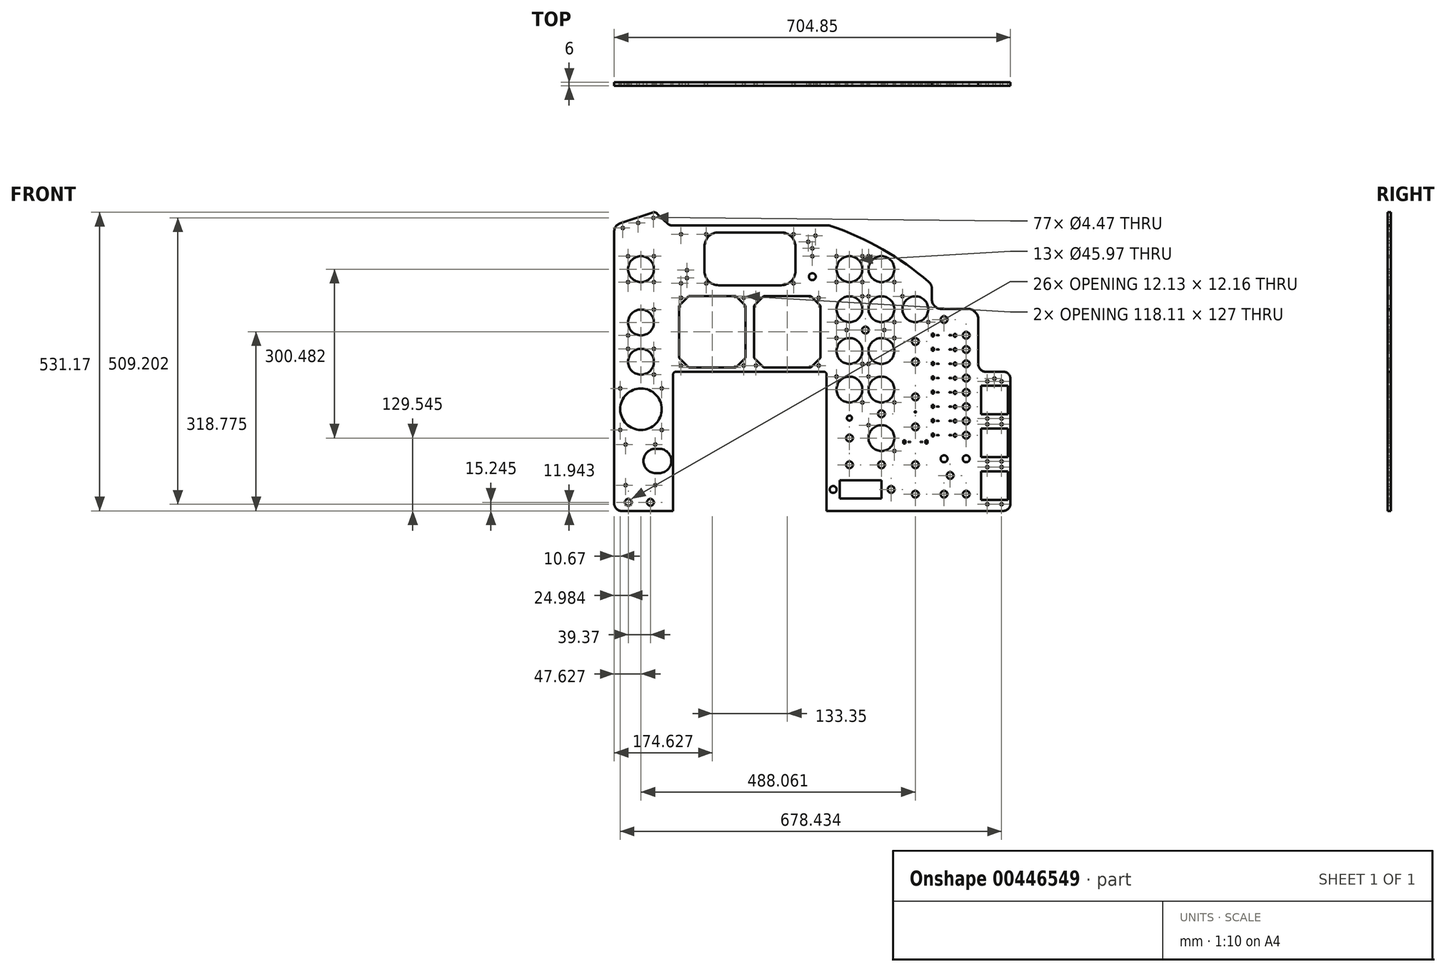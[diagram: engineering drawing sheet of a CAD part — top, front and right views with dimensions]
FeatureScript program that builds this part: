
annotation { "Feature Type Name" : "Feature", "Feature Type Description" : "" }
export const myFeature = defineFeature(function(context is Context, id is Id, definition is map)
    precondition{}
    {
        {
            var Q0;
            Q0=qCreatedBy(makeId("Front.planeOp"),FACE);
            var sketch = newSketch(context, id + "F0", { "sketchPlane" : qUnion([Q0])});
            skLineSegment(sketch, "E0", {"start": v(-241.06, -131.64) * mm, "end": v(-148.98, -131.64) * mm});
            skLineSegment(sketch, "E1", {"start": v(-148.98, -131.64) * mm, "end": v(-148.98, 110.93) * mm});
            skLineSegment(sketch, "E2", {"start": v(-143.9, 116.01) * mm, "end": v(118.99, 116.01) * mm});
            skLineSegment(sketch, "E3", {"start": v(124.07, 110.93) * mm, "end": v(124.07, -131.64) * mm});
            skLineSegment(sketch, "E4", {"start": v(124.07, -131.64) * mm, "end": v(311.4, -131.64) * mm});
            skLineSegment(sketch, "E5", {"start": v(-253.76, 255.71) * mm, "end": v(-253.76, -118.94) * mm});
            skLineSegment(sketch, "E6", {"start": v(-152.8, 376.44) * mm, "end": v(117.72, 376.44) * mm});
            skLineSegment(sketch, "E7", {"start": v(-253.76, 255.71) * mm, "end": v(-253.76, 365.43) * mm});
            skLineSegment(sketch, "E8", {"start": v(311.4, -131.64) * mm, "end": v(438.4, -131.64) * mm});
            skLineSegment(sketch, "E9", {"start": v(451.1, -118.94) * mm, "end": v(451.1, 103.31) * mm});
            skLineSegment(sketch, "E10", {"start": v(438.4, 116.01) * mm, "end": v(406.64, 116.01) * mm});
            skLineSegment(sketch, "E11", {"start": v(393.94, 128.71) * mm, "end": v(393.94, 208.72) * mm});
            skLineSegment(sketch, "E12", {"start": v(374.9, 227.77) * mm, "end": v(327.9, 227.77) * mm});
            skLineSegment(sketch, "E13", {"start": v(-243.3, 379.9) * mm, "end": v(-185.23, 399.14) * mm});
            skLineSegment(sketch, "E14", {"start": v(-157.17, 378.17) * mm, "end": v(-177.6, 397.45) * mm});
            skLineSegment(sketch, "E15", {"start": v(117.72, 376.44) * mm, "end": v(123.7, 376.44) * mm});
            skLineSegment(sketch, "E16", {"start": v(311.4, 255.71) * mm, "end": v(311.4, 263.42) * mm});
            skLineSegment(sketch, "E17", {"start": v(-253.76, 376.44) * mm, "end": v(-155.33, 376.44) * mm, "construction": true});
            skLineSegment(sketch, "E18", {"start": v(-180.91, 400.57) * mm, "end": v(-180.91, 376.44) * mm, "construction": true});
            skLineSegment(sketch, "E19", {"start": v(217.5, 323.68) * mm, "end": v(223.32, 333.8) * mm, "construction": true});
            skArc(sketch, "E20", {"start": v(305.6, 275.97) * mm, "mid": v(223.45, 333.73) * mm, "end": v(131.93, 375.07) * mm});
            skLineSegment(sketch, "E21", {"start": v(127.88, 376.44) * mm, "end": v(311.4, 270.95) * mm, "construction": true});
            skPoint(sketch, "E22.visualSharp", {"position": v(451.1, -131.64) * mm});
            skArc(sketch, "E22.filletArc", {"start": v(438.4, -131.64) * mm, "mid": v(447.37, -127.92) * mm, "end": v(451.1, -118.94) * mm});
            skPoint(sketch, "E23.visualSharp", {"position": v(451.1, 116.01) * mm});
            skArc(sketch, "E23.filletArc", {"start": v(451.1, 103.31) * mm, "mid": v(447.37, 112.3) * mm, "end": v(438.4, 116.01) * mm});
            skPoint(sketch, "E24.visualSharp", {"position": v(393.94, 116.01) * mm});
            skArc(sketch, "E24.filletArc", {"start": v(393.94, 128.71) * mm, "mid": v(397.66, 119.73) * mm, "end": v(406.64, 116.01) * mm});
            skPoint(sketch, "E25.visualSharp", {"position": v(393.94, 227.77) * mm});
            skArc(sketch, "E25.filletArc", {"start": v(393.94, 208.72) * mm, "mid": v(388.36, 222.2) * mm, "end": v(374.9, 227.77) * mm});
            skPoint(sketch, "E26.visualSharp", {"position": v(124.07, 116.01) * mm});
            skArc(sketch, "E26.filletArc", {"start": v(124.07, 110.93) * mm, "mid": v(122.58, 114.53) * mm, "end": v(118.99, 116.01) * mm});
            skPoint(sketch, "E27.visualSharp", {"position": v(-148.98, 116.01) * mm});
            skArc(sketch, "E27.filletArc", {"start": v(-143.9, 116.01) * mm, "mid": v(-147.5, 114.53) * mm, "end": v(-148.98, 110.93) * mm});
            skPoint(sketch, "E28.visualSharp", {"position": v(-253.76, -131.64) * mm});
            skArc(sketch, "E28.filletArc", {"start": v(-253.76, -118.94) * mm, "mid": v(-250.04, -127.92) * mm, "end": v(-241.06, -131.64) * mm});
            skPoint(sketch, "E29.visualSharp", {"position": v(-155.33, 376.44) * mm});
            skArc(sketch, "E29.filletArc", {"start": v(-157.17, 378.17) * mm, "mid": v(-155.15, 376.89) * mm, "end": v(-152.8, 376.44) * mm});
            skPoint(sketch, "E30.visualSharp", {"position": v(-180.91, 400.57) * mm});
            skArc(sketch, "E30.filletArc", {"start": v(-177.6, 397.45) * mm, "mid": v(-181.18, 399.35) * mm, "end": v(-185.23, 399.14) * mm});
            skPoint(sketch, "E31.visualSharp", {"position": v(-253.76, 376.44) * mm});
            skArc(sketch, "E31.filletArc", {"start": v(-243.3, 379.9) * mm, "mid": v(-250.87, 374.36) * mm, "end": v(-253.76, 365.43) * mm});
            skLineSegment(sketch, "E32", {"start": v(311.4, 255.71) * mm, "end": v(311.4, 244.28) * mm});
            skPoint(sketch, "E33.visualSharp", {"position": v(311.4, 227.77) * mm});
            skArc(sketch, "E33.filletArc", {"start": v(311.4, 244.28) * mm, "mid": v(316.23, 232.61) * mm, "end": v(327.9, 227.77) * mm});
            skPoint(sketch, "E34.visualSharp", {"position": v(311.4, 270.95) * mm});
            skArc(sketch, "E34.filletArc", {"start": v(311.4, 263.42) * mm, "mid": v(309.88, 270.33) * mm, "end": v(305.6, 275.97) * mm});
            skPoint(sketch, "E35.visualSharp", {"position": v(127.88, 376.44) * mm});
            skArc(sketch, "E35.filletArc", {"start": v(131.93, 375.07) * mm, "mid": v(127.87, 376.1) * mm, "end": v(123.7, 376.44) * mm});
            skLineSegment(sketch, "E36", {"start": v(-206.13, -131.64) * mm, "end": v(-206.13, 376.44) * mm, "construction": true});
            skCircle(sketch, "E37", {"center": v(-206.13, 49.34) * mm, "radius": 36.96 * mm});
            skCircle(sketch, "E38", {"center": v(-206.13, 133.67) * mm, "radius": 22.99 * mm});
            skCircle(sketch, "E39", {"center": v(-206.13, 203.52) * mm, "radius": 22.99 * mm});
            skCircle(sketch, "E40", {"center": v(-206.13, 298.39) * mm, "radius": 22.99 * mm});
            skLineSegment(sketch, "E41", {"start": v(164.7, -131.64) * mm, "end": v(164.7, 355.27) * mm, "construction": true});
            skLineSegment(sketch, "E42", {"start": v(221.6, -131.64) * mm, "end": v(221.6, 322.57) * mm, "construction": true});
            skLineSegment(sketch, "E43", {"start": v(281.93, -131.64) * mm, "end": v(281.93, 287.9) * mm, "construction": true});
            skCircle(sketch, "E44", {"center": v(164.7, 84.26) * mm, "radius": 22.99 * mm});
            skCircle(sketch, "E45", {"center": v(164.7, 152.84) * mm, "radius": 22.99 * mm});
            skCircle(sketch, "E46", {"center": v(221.6, 152.84) * mm, "radius": 22.99 * mm});
            skCircle(sketch, "E47", {"center": v(221.6, 84.26) * mm, "radius": 22.99 * mm});
            skCircle(sketch, "E48", {"center": v(164.7, 227.14) * mm, "radius": 22.99 * mm});
            skCircle(sketch, "E49", {"center": v(221.6, 227.14) * mm, "radius": 22.99 * mm});
            skCircle(sketch, "E50", {"center": v(164.7, 298.39) * mm, "radius": 22.99 * mm});
            skCircle(sketch, "E51", {"center": v(221.6, 298.39) * mm, "radius": 22.99 * mm});
            skCircle(sketch, "E52", {"center": v(281.93, 227.14) * mm, "radius": 22.99 * mm});
            skLineSegment(sketch, "E53", {"start": v(372.35, -131.64) * mm, "end": v(372.35, 227.77) * mm, "construction": true});
            skLineSegment(sketch, "E54", {"start": v(332.98, -131.64) * mm, "end": v(332.98, 227.77) * mm, "construction": true});
            skLineSegment(sketch, "E55", {"start": v(435.34, -131.64) * mm, "end": v(435.34, 116.01) * mm, "construction": true});
            skLineSegment(sketch, "E56", {"start": v(409.94, -131.64) * mm, "end": v(409.94, 116.01) * mm, "construction": true});
            skArc(sketch, "E57", {"start": v(378.38, 3.93) * mm, "mid": v(366.25, 2.98) * mm, "end": v(378.38, 2.03) * mm});
            skArc(sketch, "E58.0.1.0", {"start": v(378.38, 29.33) * mm, "mid": v(366.25, 28.38) * mm, "end": v(378.38, 27.43) * mm});
            skArc(sketch, "E58.0.2.0", {"start": v(378.38, 54.73) * mm, "mid": v(366.25, 53.78) * mm, "end": v(378.38, 52.83) * mm});
            skArc(sketch, "E58.0.3.0", {"start": v(378.38, 80.13) * mm, "mid": v(366.25, 79.18) * mm, "end": v(378.38, 78.23) * mm});
            skArc(sketch, "E58.0.4.0", {"start": v(378.38, 105.53) * mm, "mid": v(366.25, 104.58) * mm, "end": v(378.38, 103.63) * mm});
            skArc(sketch, "E58.0.5.0", {"start": v(378.38, 130.93) * mm, "mid": v(366.25, 129.98) * mm, "end": v(378.38, 129.03) * mm});
            skArc(sketch, "E58.0.6.0", {"start": v(378.38, 156.33) * mm, "mid": v(366.25, 155.38) * mm, "end": v(378.38, 154.43) * mm});
            skArc(sketch, "E58.0.7.0", {"start": v(378.38, 181.73) * mm, "mid": v(366.25, 180.78) * mm, "end": v(378.38, 179.83) * mm});
            skLineSegment(sketch, "E58.direction1", {"start": v(372.35, 2.98) * mm, "end": v(397.75, 2.98) * mm, "construction": true});
            skLineSegment(sketch, "E58.direction2", {"start": v(372.35, 2.98) * mm, "end": v(372.35, 28.38) * mm, "construction": true});
            skCircle(sketch, "E59", {"center": v(321.8, 2.98) * mm, "radius": 3.77 * mm, "construction": true});
            skCircle(sketch, "E60.0.1.0", {"center": v(321.8, 28.38) * mm, "radius": 3.77 * mm, "construction": true});
            skCircle(sketch, "E60.0.2.0", {"center": v(321.8, 53.78) * mm, "radius": 3.77 * mm, "construction": true});
            skCircle(sketch, "E60.0.3.0", {"center": v(321.8, 79.18) * mm, "radius": 3.77 * mm, "construction": true});
            skCircle(sketch, "E60.0.4.0", {"center": v(321.8, 104.58) * mm, "radius": 3.77 * mm, "construction": true});
            skCircle(sketch, "E60.0.5.0", {"center": v(321.8, 129.98) * mm, "radius": 3.77 * mm, "construction": true});
            skCircle(sketch, "E60.0.6.0", {"center": v(321.8, 155.38) * mm, "radius": 3.77 * mm, "construction": true});
            skCircle(sketch, "E60.0.7.0", {"center": v(321.8, 180.78) * mm, "radius": 3.77 * mm, "construction": true});
            skCircle(sketch, "E60.1.0.0", {"center": v(344.16, 2.98) * mm, "radius": 3.77 * mm, "construction": true});
            skCircle(sketch, "E60.1.1.0", {"center": v(344.16, 28.38) * mm, "radius": 3.77 * mm, "construction": true});
            skCircle(sketch, "E60.1.2.0", {"center": v(344.16, 53.78) * mm, "radius": 3.77 * mm, "construction": true});
            skCircle(sketch, "E60.1.3.0", {"center": v(344.16, 79.18) * mm, "radius": 3.77 * mm, "construction": true});
            skCircle(sketch, "E60.1.4.0", {"center": v(344.16, 104.58) * mm, "radius": 3.77 * mm, "construction": true});
            skCircle(sketch, "E60.1.5.0", {"center": v(344.16, 129.98) * mm, "radius": 3.77 * mm, "construction": true});
            skCircle(sketch, "E60.1.6.0", {"center": v(344.16, 155.38) * mm, "radius": 3.77 * mm, "construction": true});
            skCircle(sketch, "E60.1.7.0", {"center": v(344.16, 180.78) * mm, "radius": 3.77 * mm, "construction": true});
            skLineSegment(sketch, "E60.direction1", {"start": v(321.8, 2.98) * mm, "end": v(344.16, 2.98) * mm, "construction": true});
            skLineSegment(sketch, "E60.direction2", {"start": v(321.8, 2.98) * mm, "end": v(321.8, 28.38) * mm, "construction": true});
            skLineSegment(sketch, "E61.bottom", {"start": v(-68.02, 363.74) * mm, "end": v(43.1, 363.74) * mm});
            skLineSegment(sketch, "E61.top", {"start": v(-68.02, 269.76) * mm, "end": v(43.1, 269.76) * mm});
            skLineSegment(sketch, "E61.left", {"start": v(-93.42, 338.34) * mm, "end": v(-93.42, 295.16) * mm});
            skLineSegment(sketch, "E61.right", {"start": v(68.5, 338.34) * mm, "end": v(68.5, 295.16) * mm});
            skLineSegment(sketch, "E62", {"start": v(-12.46, 116.01) * mm, "end": v(-12.46, 376.44) * mm, "construction": true});
            skPoint(sketch, "E63.visualSharp", {"position": v(-93.42, 363.74) * mm});
            skArc(sketch, "E63.filletArc", {"start": v(-68.02, 363.74) * mm, "mid": v(-85.98, 356.3) * mm, "end": v(-93.42, 338.34) * mm});
            skPoint(sketch, "E64.visualSharp", {"position": v(-93.42, 269.76) * mm});
            skArc(sketch, "E64.filletArc", {"start": v(-93.42, 295.16) * mm, "mid": v(-85.98, 277.2) * mm, "end": v(-68.02, 269.76) * mm});
            skPoint(sketch, "E65.visualSharp", {"position": v(68.5, 363.74) * mm});
            skArc(sketch, "E65.filletArc", {"start": v(68.5, 338.34) * mm, "mid": v(61.07, 356.3) * mm, "end": v(43.1, 363.74) * mm});
            skPoint(sketch, "E66.visualSharp", {"position": v(68.5, 269.76) * mm});
            skArc(sketch, "E66.filletArc", {"start": v(43.1, 269.76) * mm, "mid": v(61.07, 277.2) * mm, "end": v(68.5, 295.16) * mm});
            skLineSegment(sketch, "E67", {"start": v(113.27, 123.63) * mm, "end": v(96, 123.63) * mm, "construction": true});
            skLineSegment(sketch, "E68", {"start": v(113.27, 123.63) * mm, "end": v(113.27, 140.9) * mm, "construction": true});
            skLineSegment(sketch, "E69", {"start": v(113.27, 250.63) * mm, "end": v(113.27, 233.36) * mm, "construction": true});
            skLineSegment(sketch, "E70", {"start": v(113.27, 250.63) * mm, "end": v(96, 250.63) * mm, "construction": true});
            skLineSegment(sketch, "E71", {"start": v(-4.84, 250.63) * mm, "end": v(12.43, 250.63) * mm, "construction": true});
            skLineSegment(sketch, "E72", {"start": v(-4.84, 250.63) * mm, "end": v(-4.84, 233.36) * mm, "construction": true});
            skLineSegment(sketch, "E73", {"start": v(-4.84, 123.63) * mm, "end": v(-4.84, 140.9) * mm, "construction": true});
            skLineSegment(sketch, "E74", {"start": v(-4.84, 123.63) * mm, "end": v(12.43, 123.63) * mm, "construction": true});
            skLineSegment(sketch, "E75", {"start": v(12.43, 123.63) * mm, "end": v(96, 123.63) * mm});
            skLineSegment(sketch, "E76", {"start": v(113.27, 140.9) * mm, "end": v(96, 123.63) * mm});
            skLineSegment(sketch, "E77", {"start": v(113.27, 233.36) * mm, "end": v(113.27, 140.9) * mm});
            skLineSegment(sketch, "E78", {"start": v(113.27, 233.36) * mm, "end": v(96, 250.63) * mm});
            skLineSegment(sketch, "E79", {"start": v(96, 250.63) * mm, "end": v(12.43, 250.63) * mm});
            skLineSegment(sketch, "E80", {"start": v(-4.84, 233.36) * mm, "end": v(-4.84, 140.9) * mm});
            skLineSegment(sketch, "E81", {"start": v(-4.84, 140.9) * mm, "end": v(12.43, 123.63) * mm});
            skLineSegment(sketch, "E82", {"start": v(-4.84, 233.36) * mm, "end": v(12.43, 250.63) * mm});
            skLineSegment(sketch, "E83", {"start": v(-20.08, 123.63) * mm, "end": v(-37.35, 123.63) * mm, "construction": true});
            skLineSegment(sketch, "E84", {"start": v(-20.08, 123.63) * mm, "end": v(-20.08, 140.9) * mm, "construction": true});
            skLineSegment(sketch, "E85", {"start": v(-20.08, 250.63) * mm, "end": v(-20.08, 233.36) * mm, "construction": true});
            skLineSegment(sketch, "E86", {"start": v(-20.08, 250.63) * mm, "end": v(-37.35, 250.63) * mm, "construction": true});
            skLineSegment(sketch, "E87", {"start": v(-138.19, 250.63) * mm, "end": v(-120.92, 250.63) * mm, "construction": true});
            skLineSegment(sketch, "E88", {"start": v(-138.19, 250.63) * mm, "end": v(-138.19, 233.36) * mm, "construction": true});
            skLineSegment(sketch, "E89", {"start": v(-138.19, 123.63) * mm, "end": v(-138.19, 140.9) * mm, "construction": true});
            skLineSegment(sketch, "E90", {"start": v(-138.19, 123.63) * mm, "end": v(-120.92, 123.63) * mm, "construction": true});
            skLineSegment(sketch, "E91", {"start": v(-120.92, 123.63) * mm, "end": v(-37.35, 123.63) * mm});
            skLineSegment(sketch, "E92", {"start": v(-20.08, 140.9) * mm, "end": v(-37.35, 123.63) * mm});
            skLineSegment(sketch, "E93", {"start": v(-20.08, 233.36) * mm, "end": v(-20.08, 140.9) * mm});
            skLineSegment(sketch, "E94", {"start": v(-20.08, 233.36) * mm, "end": v(-37.35, 250.63) * mm});
            skLineSegment(sketch, "E95", {"start": v(-37.35, 250.63) * mm, "end": v(-120.92, 250.63) * mm});
            skLineSegment(sketch, "E96", {"start": v(-138.19, 233.36) * mm, "end": v(-138.19, 140.9) * mm});
            skLineSegment(sketch, "E97", {"start": v(-138.19, 140.9) * mm, "end": v(-120.92, 123.63) * mm});
            skLineSegment(sketch, "E98", {"start": v(-138.19, 233.36) * mm, "end": v(-120.92, 250.63) * mm});
            skLineSegment(sketch, "E99.bottom", {"start": v(354.57, 13.97) * mm, "end": v(311.4, 13.97) * mm, "construction": true});
            skLineSegment(sketch, "E99.top", {"start": v(354.57, -8) * mm, "end": v(311.4, -8) * mm, "construction": true});
            skLineSegment(sketch, "E99.left", {"start": v(354.57, 13.97) * mm, "end": v(354.57, -8) * mm, "construction": true});
            skLineSegment(sketch, "E99.right", {"start": v(311.4, 13.97) * mm, "end": v(311.4, -8) * mm, "construction": true});
            skPoint(sketch, "E99.middle", {"position": v(332.98, 2.98) * mm});
            skLineSegment(sketch, "E100.0.1.0", {"start": v(354.57, 39.37) * mm, "end": v(311.4, 39.37) * mm, "construction": true});
            skLineSegment(sketch, "E100.0.1.1", {"start": v(354.57, 39.37) * mm, "end": v(354.57, 17.4) * mm, "construction": true});
            skLineSegment(sketch, "E100.0.1.2", {"start": v(354.57, 17.4) * mm, "end": v(311.4, 17.4) * mm, "construction": true});
            skLineSegment(sketch, "E100.0.1.3", {"start": v(311.4, 39.37) * mm, "end": v(311.4, 17.4) * mm, "construction": true});
            skLineSegment(sketch, "E100.0.2.0", {"start": v(354.57, 64.77) * mm, "end": v(311.4, 64.77) * mm, "construction": true});
            skLineSegment(sketch, "E100.0.2.1", {"start": v(354.57, 64.77) * mm, "end": v(354.57, 42.8) * mm, "construction": true});
            skLineSegment(sketch, "E100.0.2.2", {"start": v(354.57, 42.8) * mm, "end": v(311.4, 42.8) * mm, "construction": true});
            skLineSegment(sketch, "E100.0.2.3", {"start": v(311.4, 64.77) * mm, "end": v(311.4, 42.8) * mm, "construction": true});
            skLineSegment(sketch, "E100.0.3.0", {"start": v(354.57, 90.17) * mm, "end": v(311.4, 90.17) * mm, "construction": true});
            skLineSegment(sketch, "E100.0.3.1", {"start": v(354.57, 90.17) * mm, "end": v(354.57, 68.2) * mm, "construction": true});
            skLineSegment(sketch, "E100.0.3.2", {"start": v(354.57, 68.2) * mm, "end": v(311.4, 68.2) * mm, "construction": true});
            skLineSegment(sketch, "E100.0.3.3", {"start": v(311.4, 90.17) * mm, "end": v(311.4, 68.2) * mm, "construction": true});
            skLineSegment(sketch, "E100.0.4.0", {"start": v(354.57, 115.57) * mm, "end": v(311.4, 115.57) * mm, "construction": true});
            skLineSegment(sketch, "E100.0.4.1", {"start": v(354.57, 115.57) * mm, "end": v(354.57, 93.6) * mm, "construction": true});
            skLineSegment(sketch, "E100.0.4.2", {"start": v(354.57, 93.6) * mm, "end": v(311.4, 93.6) * mm, "construction": true});
            skLineSegment(sketch, "E100.0.4.3", {"start": v(311.4, 115.57) * mm, "end": v(311.4, 93.6) * mm, "construction": true});
            skLineSegment(sketch, "E100.0.5.0", {"start": v(354.57, 140.97) * mm, "end": v(311.4, 140.97) * mm, "construction": true});
            skLineSegment(sketch, "E100.0.5.1", {"start": v(354.57, 140.97) * mm, "end": v(354.57, 119) * mm, "construction": true});
            skLineSegment(sketch, "E100.0.5.2", {"start": v(354.57, 119) * mm, "end": v(311.4, 119) * mm, "construction": true});
            skLineSegment(sketch, "E100.0.5.3", {"start": v(311.4, 140.97) * mm, "end": v(311.4, 119) * mm, "construction": true});
            skLineSegment(sketch, "E100.0.6.0", {"start": v(354.57, 166.37) * mm, "end": v(311.4, 166.37) * mm, "construction": true});
            skLineSegment(sketch, "E100.0.6.1", {"start": v(354.57, 166.37) * mm, "end": v(354.57, 144.4) * mm, "construction": true});
            skLineSegment(sketch, "E100.0.6.2", {"start": v(354.57, 144.4) * mm, "end": v(311.4, 144.4) * mm, "construction": true});
            skLineSegment(sketch, "E100.0.6.3", {"start": v(311.4, 166.37) * mm, "end": v(311.4, 144.4) * mm, "construction": true});
            skLineSegment(sketch, "E100.0.7.0", {"start": v(354.57, 191.77) * mm, "end": v(311.4, 191.77) * mm, "construction": true});
            skLineSegment(sketch, "E100.0.7.1", {"start": v(354.57, 191.77) * mm, "end": v(354.57, 169.8) * mm, "construction": true});
            skLineSegment(sketch, "E100.0.7.2", {"start": v(354.57, 169.8) * mm, "end": v(311.4, 169.8) * mm, "construction": true});
            skLineSegment(sketch, "E100.0.7.3", {"start": v(311.4, 191.77) * mm, "end": v(311.4, 169.8) * mm, "construction": true});
            skLineSegment(sketch, "E100.direction1", {"start": v(311.4, -8) * mm, "end": v(336.8, -8) * mm, "construction": true});
            skLineSegment(sketch, "E100.direction2", {"start": v(311.4, -8) * mm, "end": v(311.4, 17.4) * mm, "construction": true});
            skLineSegment(sketch, "E101.bottom", {"start": v(421.12, -112.08) * mm, "end": v(398.77, -112.08) * mm});
            skLineSegment(sketch, "E101.top", {"start": v(421.12, -61.28) * mm, "end": v(398.77, -61.28) * mm});
            skLineSegment(sketch, "E101.right", {"start": v(398.77, -112.08) * mm, "end": v(398.77, -61.28) * mm});
            skPoint(sketch, "E101.middle", {"position": v(409.94, -86.68) * mm});
            skPoint(sketch, "E102.0.1.0", {"position": v(409.94, -10.48) * mm});
            skLineSegment(sketch, "E102.0.1.2", {"start": v(398.77, -35.88) * mm, "end": v(398.77, 14.92) * mm});
            skPoint(sketch, "E102.0.2.0", {"position": v(409.94, 65.72) * mm});
            skLineSegment(sketch, "E102.0.2.2", {"start": v(398.77, 40.32) * mm, "end": v(398.77, 91.12) * mm});
            skPoint(sketch, "E102.1.0.0", {"position": v(435.34, -86.68) * mm});
            skLineSegment(sketch, "E102.1.0.1", {"start": v(446.52, -112.08) * mm, "end": v(446.52, -61.28) * mm});
            skPoint(sketch, "E102.1.1.0", {"position": v(435.34, -10.48) * mm});
            skLineSegment(sketch, "E102.1.1.1", {"start": v(446.52, -35.88) * mm, "end": v(446.52, 14.92) * mm});
            skPoint(sketch, "E102.1.2.0", {"position": v(435.34, 65.72) * mm});
            skLineSegment(sketch, "E102.1.2.1", {"start": v(446.52, 40.32) * mm, "end": v(446.52, 91.12) * mm});
            skLineSegment(sketch, "E102.direction1", {"start": v(398.77, -112.08) * mm, "end": v(424.17, -112.08) * mm, "construction": true});
            skLineSegment(sketch, "E102.direction2", {"start": v(398.77, -112.08) * mm, "end": v(398.77, -35.88) * mm, "construction": true});
            skArc(sketch, "E103", {"start": v(-183.34, -115.45) * mm, "mid": v(-195.47, -116.4) * mm, "end": v(-183.34, -117.35) * mm});
            skArc(sketch, "E104", {"start": v(-222.71, -115.45) * mm, "mid": v(-234.84, -116.4) * mm, "end": v(-222.71, -117.35) * mm});
            skLineSegment(sketch, "E105", {"start": v(-148.98, -116.4) * mm, "end": v(-253.76, -116.4) * mm, "construction": true});
            skLineSegment(sketch, "E106", {"start": v(124.07, 84.26) * mm, "end": v(281.93, 84.26) * mm, "construction": true});
            skLineSegment(sketch, "E107", {"start": v(281.93, 152.84) * mm, "end": v(125.15, 152.84) * mm, "construction": true});
            skLineSegment(sketch, "E108", {"start": v(281.93, 227.14) * mm, "end": v(116.2, 227.14) * mm, "construction": true});
            skArc(sketch, "E109", {"start": v(339, 209.67) * mm, "mid": v(326.88, 208.72) * mm, "end": v(339, 207.77) * mm});
            skLineSegment(sketch, "E110", {"start": v(281.93, -101.92) * mm, "end": v(451.1, -101.92) * mm, "construction": true});
            skArc(sketch, "E111", {"start": v(287.95, -100.97) * mm, "mid": v(275.83, -101.92) * mm, "end": v(287.95, -102.87) * mm});
            skArc(sketch, "E112", {"start": v(339, -100.97) * mm, "mid": v(326.88, -101.92) * mm, "end": v(339, -102.87) * mm});
            skArc(sketch, "E113", {"start": v(378.38, -100.97) * mm, "mid": v(366.25, -101.92) * mm, "end": v(378.38, -102.87) * mm});
            skLineSegment(sketch, "E114", {"start": v(124.07, -49.6) * mm, "end": v(281.93, -49.6) * mm, "construction": true});
            skLineSegment(sketch, "E115", {"start": v(124.07, -93.54) * mm, "end": v(281.93, -93.54) * mm, "construction": true});
            skArc(sketch, "E116", {"start": v(170.73, -48.64) * mm, "mid": v(158.6, -49.6) * mm, "end": v(170.73, -50.54) * mm});
            skArc(sketch, "E117", {"start": v(287.95, -48.64) * mm, "mid": v(275.83, -49.6) * mm, "end": v(287.95, -50.54) * mm});
            skLineSegment(sketch, "E118.bottom", {"start": v(260.34, 2.03) * mm, "end": v(303.52, 2.03) * mm, "construction": true});
            skLineSegment(sketch, "E118.top", {"start": v(260.34, -19.94) * mm, "end": v(303.52, -19.94) * mm, "construction": true});
            skLineSegment(sketch, "E118.left", {"start": v(260.34, 2.03) * mm, "end": v(260.34, -19.94) * mm, "construction": true});
            skLineSegment(sketch, "E118.right", {"start": v(303.52, 2.03) * mm, "end": v(303.52, -19.94) * mm, "construction": true});
            skPoint(sketch, "E118.middle", {"position": v(281.93, -8.95) * mm});
            skLineSegment(sketch, "E119", {"start": v(281.93, -8.95) * mm, "end": v(303.52, -8.95) * mm, "construction": true});
            skLineSegment(sketch, "E120", {"start": v(281.93, -8.95) * mm, "end": v(260.34, -8.95) * mm, "construction": true});
            skCircle(sketch, "E121", {"center": v(271.13, -8.95) * mm, "radius": 3.77 * mm, "construction": true});
            skCircle(sketch, "E122", {"center": v(292.72, -8.95) * mm, "radius": 3.77 * mm, "construction": true});
            skArc(sketch, "E123", {"start": v(287.95, 18.67) * mm, "mid": v(275.83, 17.72) * mm, "end": v(287.95, 16.77) * mm});
            skCircle(sketch, "E124", {"center": v(281.93, 44.39) * mm, "radius": 1.27 * mm});
            skArc(sketch, "E125", {"start": v(287.95, 72) * mm, "mid": v(275.83, 71.06) * mm, "end": v(287.95, 70.1) * mm});
            skLineSegment(sketch, "E126", {"start": v(451.1, -38.93) * mm, "end": v(281.93, -38.93) * mm, "construction": true});
            skLineSegment(sketch, "E127", {"start": v(164.7, 190) * mm, "end": v(221.6, 190) * mm, "construction": true});
            skLineSegment(sketch, "E128", {"start": v(164.7, 227.14) * mm, "end": v(164.7, 152.84) * mm, "construction": true});
            skArc(sketch, "E129", {"start": v(199.18, 190.94) * mm, "mid": v(187.06, 190) * mm, "end": v(199.18, 189.04) * mm});
            skArc(sketch, "E130", {"start": v(287.95, 170.56) * mm, "mid": v(275.83, 169.6) * mm, "end": v(287.95, 168.66) * mm});
            skArc(sketch, "E131", {"start": v(287.95, 134.24) * mm, "mid": v(275.83, 133.29) * mm, "end": v(287.95, 132.34) * mm});
            skArc(sketch, "E132", {"start": v(227.63, 42.03) * mm, "mid": v(215.5, 41.08) * mm, "end": v(227.63, 40.13) * mm});
            skLineSegment(sketch, "E133.bottom", {"start": v(221.6, -109.66) * mm, "end": v(147.44, -109.66) * mm});
            skLineSegment(sketch, "E133.top", {"start": v(221.6, -77.4) * mm, "end": v(147.44, -77.4) * mm});
            skLineSegment(sketch, "E133.left", {"start": v(221.6, -109.66) * mm, "end": v(221.6, -77.4) * mm});
            skLineSegment(sketch, "E133.right", {"start": v(147.44, -109.66) * mm, "end": v(147.44, -77.4) * mm});
            skPoint(sketch, "E133.middle", {"position": v(184.52, -93.54) * mm});
            skArc(sketch, "E134", {"start": v(244.9, -92.59) * mm, "mid": v(232.78, -93.54) * mm, "end": v(244.9, -94.49) * mm});
            skCircle(sketch, "E135", {"center": v(135.75, -93.54) * mm, "radius": 6.15 * mm});
            skArc(sketch, "E136", {"start": v(349.93, -67.7) * mm, "mid": v(337.8, -68.64) * mm, "end": v(349.93, -69.6) * mm});
            skArc(sketch, "E137", {"start": v(227.63, -48.64) * mm, "mid": v(215.5, -49.6) * mm, "end": v(227.63, -50.54) * mm});
            skCircle(sketch, "E138", {"center": v(332.98, -38.93) * mm, "radius": 6.15 * mm});
            skCircle(sketch, "E139", {"center": v(372.35, -38.93) * mm, "radius": 6.15 * mm});
            skCircle(sketch, "E140", {"center": v(98.67, 285) * mm, "radius": 6.15 * mm});
            skLineSegment(sketch, "E141", {"start": v(124.07, -2.1) * mm, "end": v(221.6, -2.1) * mm, "construction": true});
            skArc(sketch, "E142", {"start": v(170.73, -1.15) * mm, "mid": v(158.6, -2.1) * mm, "end": v(170.73, -3.05) * mm});
            skCircle(sketch, "E143", {"center": v(221.6, -2.1) * mm, "radius": 22.99 * mm});
            skLineSegment(sketch, "E144", {"start": v(-253.76, -42.74) * mm, "end": v(-148.98, -42.74) * mm, "construction": true});
            skLineSegment(sketch, "E145.bottom", {"start": v(-180.1, -21.15) * mm, "end": v(-173.75, -21.15) * mm, "construction": true});
            skLineSegment(sketch, "E145.top", {"start": v(-180.1, -64.33) * mm, "end": v(-173.75, -64.33) * mm, "construction": true});
            skLineSegment(sketch, "E145.left", {"start": v(-180.1, -21.15) * mm, "end": v(-180.1, -64.33) * mm, "construction": true});
            skLineSegment(sketch, "E145.right", {"start": v(-173.75, -21.15) * mm, "end": v(-173.75, -64.33) * mm, "construction": true});
            skPoint(sketch, "E145.middle", {"position": v(-176.92, -42.74) * mm});
            skArc(sketch, "E146", {"start": v(-173.75, -21.15) * mm, "mid": v(-152.16, -42.74) * mm, "end": v(-173.75, -64.33) * mm});
            skArc(sketch, "E147", {"start": v(-180.1, -21.15) * mm, "mid": v(-201.69, -42.74) * mm, "end": v(-180.1, -64.33) * mm});
            skLineSegment(sketch, "E148", {"start": v(-180.1, -21.15) * mm, "end": v(-173.75, -21.15) * mm});
            skLineSegment(sketch, "E149", {"start": v(-180.1, -64.33) * mm, "end": v(-173.75, -64.33) * mm});
            skCircle(sketch, "E150", {"center": v(164.7, 33.46) * mm, "radius": 4.5 * mm});
            skLineSegment(sketch, "E151", {"start": v(311.4, 244.28) * mm, "end": v(311.4, -131.64) * mm, "construction": true});
            skLineSegment(sketch, "E152", {"start": v(311.4, 255.71) * mm, "end": v(-253.76, 255.71) * mm});
            skCircle(sketch, "E153", {"center": v(272.4, -8.95) * mm, "radius": 0.5 * mm});
            skCircle(sketch, "E154", {"center": v(269.86, -8.95) * mm, "radius": 0.5 * mm});
            skCircle(sketch, "E155", {"center": v(294, -8.95) * mm, "radius": 0.5 * mm});
            skCircle(sketch, "E156", {"center": v(291.45, -8.95) * mm, "radius": 0.5 * mm});
            skCircle(sketch, "E157", {"center": v(323.08, 2.98) * mm, "radius": 0.5 * mm});
            skCircle(sketch, "E158", {"center": v(320.54, 2.98) * mm, "radius": 0.5 * mm});
            skCircle(sketch, "E159.0.1.0", {"center": v(320.54, 28.38) * mm, "radius": 0.5 * mm});
            skCircle(sketch, "E159.0.1.1", {"center": v(323.08, 28.38) * mm, "radius": 0.5 * mm});
            skCircle(sketch, "E159.0.2.0", {"center": v(320.54, 53.78) * mm, "radius": 0.5 * mm});
            skCircle(sketch, "E159.0.2.1", {"center": v(323.08, 53.78) * mm, "radius": 0.5 * mm});
            skCircle(sketch, "E159.0.3.0", {"center": v(320.54, 79.18) * mm, "radius": 0.5 * mm});
            skCircle(sketch, "E159.0.3.1", {"center": v(323.08, 79.18) * mm, "radius": 0.5 * mm});
            skCircle(sketch, "E159.0.4.0", {"center": v(320.54, 104.58) * mm, "radius": 0.5 * mm});
            skCircle(sketch, "E159.0.4.1", {"center": v(323.08, 104.58) * mm, "radius": 0.5 * mm});
            skCircle(sketch, "E159.0.5.0", {"center": v(320.54, 129.98) * mm, "radius": 0.5 * mm});
            skCircle(sketch, "E159.0.5.1", {"center": v(323.08, 129.98) * mm, "radius": 0.5 * mm});
            skCircle(sketch, "E159.0.6.0", {"center": v(320.54, 155.38) * mm, "radius": 0.5 * mm});
            skCircle(sketch, "E159.0.6.1", {"center": v(323.08, 155.38) * mm, "radius": 0.5 * mm});
            skCircle(sketch, "E159.0.7.0", {"center": v(320.54, 180.78) * mm, "radius": 0.5 * mm});
            skCircle(sketch, "E159.0.7.1", {"center": v(323.08, 180.78) * mm, "radius": 0.5 * mm});
            skCircle(sketch, "E159.1.0.0", {"center": v(342.89, 2.98) * mm, "radius": 0.5 * mm});
            skCircle(sketch, "E159.1.0.1", {"center": v(345.43, 2.98) * mm, "radius": 0.5 * mm});
            skCircle(sketch, "E159.1.1.0", {"center": v(342.89, 28.38) * mm, "radius": 0.5 * mm});
            skCircle(sketch, "E159.1.1.1", {"center": v(345.43, 28.38) * mm, "radius": 0.5 * mm});
            skCircle(sketch, "E159.1.2.0", {"center": v(342.89, 53.78) * mm, "radius": 0.5 * mm});
            skCircle(sketch, "E159.1.2.1", {"center": v(345.43, 53.78) * mm, "radius": 0.5 * mm});
            skCircle(sketch, "E159.1.3.0", {"center": v(342.89, 79.18) * mm, "radius": 0.5 * mm});
            skCircle(sketch, "E159.1.3.1", {"center": v(345.43, 79.18) * mm, "radius": 0.5 * mm});
            skCircle(sketch, "E159.1.4.0", {"center": v(342.89, 104.58) * mm, "radius": 0.5 * mm});
            skCircle(sketch, "E159.1.4.1", {"center": v(345.43, 104.58) * mm, "radius": 0.5 * mm});
            skCircle(sketch, "E159.1.5.0", {"center": v(342.89, 129.98) * mm, "radius": 0.5 * mm});
            skCircle(sketch, "E159.1.5.1", {"center": v(345.43, 129.98) * mm, "radius": 0.5 * mm});
            skCircle(sketch, "E159.1.6.0", {"center": v(342.89, 155.38) * mm, "radius": 0.5 * mm});
            skCircle(sketch, "E159.1.6.1", {"center": v(345.43, 155.38) * mm, "radius": 0.5 * mm});
            skCircle(sketch, "E159.1.7.0", {"center": v(342.89, 180.78) * mm, "radius": 0.5 * mm});
            skCircle(sketch, "E159.1.7.1", {"center": v(345.43, 180.78) * mm, "radius": 0.5 * mm});
            skLineSegment(sketch, "E159.direction1", {"start": v(320.54, 2.98) * mm, "end": v(342.89, 2.98) * mm, "construction": true});
            skLineSegment(sketch, "E159.direction2", {"start": v(320.54, 2.98) * mm, "end": v(320.54, 28.38) * mm, "construction": true});
            skLineSegment(sketch, "E160.bottom", {"start": v(303.5, -11.52) * mm, "end": v(299.7, -11.52) * mm});
            skLineSegment(sketch, "E160.top", {"start": v(303.5, -6.39) * mm, "end": v(299.7, -6.39) * mm});
            skLineSegment(sketch, "E160.left", {"start": v(303.5, -11.52) * mm, "end": v(303.5, -6.39) * mm});
            skLineSegment(sketch, "E160.right", {"start": v(299.7, -11.52) * mm, "end": v(299.7, -6.39) * mm});
            skPoint(sketch, "E160.middle", {"position": v(301.6, -8.95) * mm});
            skLineSegment(sketch, "E161.bottom", {"start": v(264.16, -11.52) * mm, "end": v(260.35, -11.52) * mm});
            skLineSegment(sketch, "E161.top", {"start": v(264.16, -6.39) * mm, "end": v(260.35, -6.39) * mm});
            skLineSegment(sketch, "E161.left", {"start": v(264.16, -11.52) * mm, "end": v(264.16, -6.39) * mm});
            skLineSegment(sketch, "E161.right", {"start": v(260.35, -11.52) * mm, "end": v(260.35, -6.39) * mm});
            skPoint(sketch, "E161.middle", {"position": v(262.25, -8.95) * mm});
            skLineSegment(sketch, "E162.bottom", {"start": v(350.76, 5.55) * mm, "end": v(354.57, 5.55) * mm});
            skLineSegment(sketch, "E162.top", {"start": v(350.76, 0.42) * mm, "end": v(354.57, 0.42) * mm});
            skLineSegment(sketch, "E162.left", {"start": v(350.76, 5.55) * mm, "end": v(350.76, 0.42) * mm});
            skLineSegment(sketch, "E162.right", {"start": v(354.57, 5.55) * mm, "end": v(354.57, 0.42) * mm});
            skPoint(sketch, "E162.middle", {"position": v(352.66, 2.98) * mm});
            skLineSegment(sketch, "E163.bottom", {"start": v(311.4, 0.62) * mm, "end": v(315.21, 0.62) * mm});
            skLineSegment(sketch, "E163.top", {"start": v(311.4, 5.75) * mm, "end": v(315.21, 5.75) * mm});
            skLineSegment(sketch, "E163.left", {"start": v(311.4, 0.62) * mm, "end": v(311.4, 5.75) * mm});
            skLineSegment(sketch, "E163.right", {"start": v(315.21, 0.62) * mm, "end": v(315.21, 5.75) * mm});
            skPoint(sketch, "E163.middle", {"position": v(313.3, 3.19) * mm});
            skLineSegment(sketch, "E164.0.1.0", {"start": v(311.4, 26.02) * mm, "end": v(315.21, 26.02) * mm});
            skPoint(sketch, "E164.0.1.1", {"position": v(313.3, 28.59) * mm});
            skLineSegment(sketch, "E164.0.1.2", {"start": v(315.21, 26.02) * mm, "end": v(315.21, 31.15) * mm});
            skLineSegment(sketch, "E164.0.1.3", {"start": v(311.4, 31.15) * mm, "end": v(315.21, 31.15) * mm});
            skLineSegment(sketch, "E164.0.1.4", {"start": v(311.4, 26.02) * mm, "end": v(311.4, 31.15) * mm});
            skPoint(sketch, "E164.0.1.5", {"position": v(352.66, 28.38) * mm});
            skLineSegment(sketch, "E164.0.1.6", {"start": v(350.76, 30.95) * mm, "end": v(350.76, 25.82) * mm});
            skLineSegment(sketch, "E164.0.1.7", {"start": v(350.76, 25.82) * mm, "end": v(354.57, 25.82) * mm});
            skLineSegment(sketch, "E164.0.1.8", {"start": v(350.76, 30.95) * mm, "end": v(354.57, 30.95) * mm});
            skLineSegment(sketch, "E164.0.1.9", {"start": v(354.57, 30.95) * mm, "end": v(354.57, 25.82) * mm});
            skLineSegment(sketch, "E164.0.2.0", {"start": v(311.4, 51.42) * mm, "end": v(315.21, 51.42) * mm});
            skPoint(sketch, "E164.0.2.1", {"position": v(313.3, 53.99) * mm});
            skLineSegment(sketch, "E164.0.2.2", {"start": v(315.21, 51.42) * mm, "end": v(315.21, 56.55) * mm});
            skLineSegment(sketch, "E164.0.2.3", {"start": v(311.4, 56.55) * mm, "end": v(315.21, 56.55) * mm});
            skLineSegment(sketch, "E164.0.2.4", {"start": v(311.4, 51.42) * mm, "end": v(311.4, 56.55) * mm});
            skPoint(sketch, "E164.0.2.5", {"position": v(352.66, 53.78) * mm});
            skLineSegment(sketch, "E164.0.2.6", {"start": v(350.76, 56.35) * mm, "end": v(350.76, 51.22) * mm});
            skLineSegment(sketch, "E164.0.2.7", {"start": v(350.76, 51.22) * mm, "end": v(354.57, 51.22) * mm});
            skLineSegment(sketch, "E164.0.2.8", {"start": v(350.76, 56.35) * mm, "end": v(354.57, 56.35) * mm});
            skLineSegment(sketch, "E164.0.2.9", {"start": v(354.57, 56.35) * mm, "end": v(354.57, 51.22) * mm});
            skLineSegment(sketch, "E164.0.3.0", {"start": v(311.4, 76.82) * mm, "end": v(315.21, 76.82) * mm});
            skPoint(sketch, "E164.0.3.1", {"position": v(313.3, 79.39) * mm});
            skLineSegment(sketch, "E164.0.3.2", {"start": v(315.21, 76.82) * mm, "end": v(315.21, 81.95) * mm});
            skLineSegment(sketch, "E164.0.3.3", {"start": v(311.4, 81.95) * mm, "end": v(315.21, 81.95) * mm});
            skLineSegment(sketch, "E164.0.3.4", {"start": v(311.4, 76.82) * mm, "end": v(311.4, 81.95) * mm});
            skPoint(sketch, "E164.0.3.5", {"position": v(352.66, 79.18) * mm});
            skLineSegment(sketch, "E164.0.3.6", {"start": v(350.76, 81.75) * mm, "end": v(350.76, 76.62) * mm});
            skLineSegment(sketch, "E164.0.3.7", {"start": v(350.76, 76.62) * mm, "end": v(354.57, 76.62) * mm});
            skLineSegment(sketch, "E164.0.3.8", {"start": v(350.76, 81.75) * mm, "end": v(354.57, 81.75) * mm});
            skLineSegment(sketch, "E164.0.3.9", {"start": v(354.57, 81.75) * mm, "end": v(354.57, 76.62) * mm});
            skLineSegment(sketch, "E164.0.4.0", {"start": v(311.4, 102.22) * mm, "end": v(315.21, 102.22) * mm});
            skPoint(sketch, "E164.0.4.1", {"position": v(313.3, 104.79) * mm});
            skLineSegment(sketch, "E164.0.4.2", {"start": v(315.21, 102.22) * mm, "end": v(315.21, 107.35) * mm});
            skLineSegment(sketch, "E164.0.4.3", {"start": v(311.4, 107.35) * mm, "end": v(315.21, 107.35) * mm});
            skLineSegment(sketch, "E164.0.4.4", {"start": v(311.4, 102.22) * mm, "end": v(311.4, 107.35) * mm});
            skPoint(sketch, "E164.0.4.5", {"position": v(352.66, 104.58) * mm});
            skLineSegment(sketch, "E164.0.4.6", {"start": v(350.76, 107.15) * mm, "end": v(350.76, 102.02) * mm});
            skLineSegment(sketch, "E164.0.4.7", {"start": v(350.76, 102.02) * mm, "end": v(354.57, 102.02) * mm});
            skLineSegment(sketch, "E164.0.4.8", {"start": v(350.76, 107.15) * mm, "end": v(354.57, 107.15) * mm});
            skLineSegment(sketch, "E164.0.4.9", {"start": v(354.57, 107.15) * mm, "end": v(354.57, 102.02) * mm});
            skLineSegment(sketch, "E164.0.5.0", {"start": v(311.4, 127.62) * mm, "end": v(315.21, 127.62) * mm});
            skPoint(sketch, "E164.0.5.1", {"position": v(313.3, 130.19) * mm});
            skLineSegment(sketch, "E164.0.5.2", {"start": v(315.21, 127.62) * mm, "end": v(315.21, 132.75) * mm});
            skLineSegment(sketch, "E164.0.5.3", {"start": v(311.4, 132.75) * mm, "end": v(315.21, 132.75) * mm});
            skLineSegment(sketch, "E164.0.5.4", {"start": v(311.4, 127.62) * mm, "end": v(311.4, 132.75) * mm});
            skPoint(sketch, "E164.0.5.5", {"position": v(352.66, 129.98) * mm});
            skLineSegment(sketch, "E164.0.5.6", {"start": v(350.76, 132.55) * mm, "end": v(350.76, 127.42) * mm});
            skLineSegment(sketch, "E164.0.5.7", {"start": v(350.76, 127.42) * mm, "end": v(354.57, 127.42) * mm});
            skLineSegment(sketch, "E164.0.5.8", {"start": v(350.76, 132.55) * mm, "end": v(354.57, 132.55) * mm});
            skLineSegment(sketch, "E164.0.5.9", {"start": v(354.57, 132.55) * mm, "end": v(354.57, 127.42) * mm});
            skLineSegment(sketch, "E164.0.6.0", {"start": v(311.4, 153.02) * mm, "end": v(315.21, 153.02) * mm});
            skPoint(sketch, "E164.0.6.1", {"position": v(313.3, 155.59) * mm});
            skLineSegment(sketch, "E164.0.6.2", {"start": v(315.21, 153.02) * mm, "end": v(315.21, 158.15) * mm});
            skLineSegment(sketch, "E164.0.6.3", {"start": v(311.4, 158.15) * mm, "end": v(315.21, 158.15) * mm});
            skLineSegment(sketch, "E164.0.6.4", {"start": v(311.4, 153.02) * mm, "end": v(311.4, 158.15) * mm});
            skPoint(sketch, "E164.0.6.5", {"position": v(352.66, 155.38) * mm});
            skLineSegment(sketch, "E164.0.6.6", {"start": v(350.76, 157.95) * mm, "end": v(350.76, 152.82) * mm});
            skLineSegment(sketch, "E164.0.6.7", {"start": v(350.76, 152.82) * mm, "end": v(354.57, 152.82) * mm});
            skLineSegment(sketch, "E164.0.6.8", {"start": v(350.76, 157.95) * mm, "end": v(354.57, 157.95) * mm});
            skLineSegment(sketch, "E164.0.6.9", {"start": v(354.57, 157.95) * mm, "end": v(354.57, 152.82) * mm});
            skLineSegment(sketch, "E164.0.7.0", {"start": v(311.4, 178.42) * mm, "end": v(315.21, 178.42) * mm});
            skPoint(sketch, "E164.0.7.1", {"position": v(313.3, 180.99) * mm});
            skLineSegment(sketch, "E164.0.7.2", {"start": v(315.21, 178.42) * mm, "end": v(315.21, 183.55) * mm});
            skLineSegment(sketch, "E164.0.7.3", {"start": v(311.4, 183.55) * mm, "end": v(315.21, 183.55) * mm});
            skLineSegment(sketch, "E164.0.7.4", {"start": v(311.4, 178.42) * mm, "end": v(311.4, 183.55) * mm});
            skPoint(sketch, "E164.0.7.5", {"position": v(352.66, 180.78) * mm});
            skLineSegment(sketch, "E164.0.7.6", {"start": v(350.76, 183.35) * mm, "end": v(350.76, 178.22) * mm});
            skLineSegment(sketch, "E164.0.7.7", {"start": v(350.76, 178.22) * mm, "end": v(354.57, 178.22) * mm});
            skLineSegment(sketch, "E164.0.7.8", {"start": v(350.76, 183.35) * mm, "end": v(354.57, 183.35) * mm});
            skLineSegment(sketch, "E164.0.7.9", {"start": v(354.57, 183.35) * mm, "end": v(354.57, 178.22) * mm});
            skLineSegment(sketch, "E164.direction1", {"start": v(311.4, 0.62) * mm, "end": v(336.8, 0.62) * mm, "construction": true});
            skLineSegment(sketch, "E164.direction2", {"start": v(311.4, 0.62) * mm, "end": v(311.4, 26.02) * mm, "construction": true});
            skLineSegment(sketch, "E165.bottom", {"start": v(244.6, -25.08) * mm, "end": v(198.62, -25.08) * mm, "construction": true});
            skLineSegment(sketch, "E165.top", {"start": v(244.6, 20.9) * mm, "end": v(198.62, 20.9) * mm, "construction": true});
            skLineSegment(sketch, "E165.left", {"start": v(244.6, -25.08) * mm, "end": v(244.6, 20.9) * mm, "construction": true});
            skLineSegment(sketch, "E165.right", {"start": v(198.62, -25.08) * mm, "end": v(198.62, 20.9) * mm, "construction": true});
            skCircle(sketch, "E166", {"center": v(244.6, -25.08) * mm, "radius": 2.24 * mm});
            skCircle(sketch, "E167", {"center": v(198.62, 20.9) * mm, "radius": 2.24 * mm});
            skLineSegment(sketch, "E168.bottom", {"start": v(244.6, 61.28) * mm, "end": v(198.62, 61.28) * mm, "construction": true});
            skLineSegment(sketch, "E168.top", {"start": v(244.6, 107.25) * mm, "end": v(198.62, 107.25) * mm, "construction": true});
            skLineSegment(sketch, "E168.left", {"start": v(244.6, 61.28) * mm, "end": v(244.6, 107.25) * mm, "construction": true});
            skLineSegment(sketch, "E168.right", {"start": v(198.62, 61.28) * mm, "end": v(198.62, 107.25) * mm, "construction": true});
            skLineSegment(sketch, "E169.bottom", {"start": v(187.7, 61.28) * mm, "end": v(141.72, 61.28) * mm, "construction": true});
            skLineSegment(sketch, "E169.top", {"start": v(187.7, 107.25) * mm, "end": v(141.72, 107.25) * mm, "construction": true});
            skLineSegment(sketch, "E169.left", {"start": v(187.7, 61.28) * mm, "end": v(187.7, 107.25) * mm, "construction": true});
            skLineSegment(sketch, "E169.right", {"start": v(141.72, 61.28) * mm, "end": v(141.72, 107.25) * mm, "construction": true});
            skCircle(sketch, "E170", {"center": v(244.6, 61.28) * mm, "radius": 2.24 * mm});
            skCircle(sketch, "E171", {"center": v(198.62, 107.25) * mm, "radius": 2.24 * mm});
            skCircle(sketch, "E172", {"center": v(187.7, 61.28) * mm, "radius": 2.24 * mm});
            skCircle(sketch, "E173", {"center": v(141.72, 107.25) * mm, "radius": 2.24 * mm});
            skLineSegment(sketch, "E174.bottom", {"start": v(244.6, 129.86) * mm, "end": v(198.62, 129.86) * mm, "construction": true});
            skLineSegment(sketch, "E174.top", {"start": v(244.6, 175.83) * mm, "end": v(198.62, 175.83) * mm, "construction": true});
            skLineSegment(sketch, "E174.left", {"start": v(244.6, 129.86) * mm, "end": v(244.6, 175.83) * mm, "construction": true});
            skLineSegment(sketch, "E174.right", {"start": v(198.62, 129.86) * mm, "end": v(198.62, 175.83) * mm, "construction": true});
            skLineSegment(sketch, "E175.bottom", {"start": v(187.7, 129.86) * mm, "end": v(141.72, 129.86) * mm, "construction": true});
            skLineSegment(sketch, "E175.top", {"start": v(187.7, 175.83) * mm, "end": v(141.72, 175.83) * mm, "construction": true});
            skLineSegment(sketch, "E175.left", {"start": v(187.7, 129.86) * mm, "end": v(187.7, 175.83) * mm, "construction": true});
            skLineSegment(sketch, "E175.right", {"start": v(141.72, 129.86) * mm, "end": v(141.72, 175.83) * mm, "construction": true});
            skCircle(sketch, "E176", {"center": v(198.62, 129.86) * mm, "radius": 2.24 * mm});
            skCircle(sketch, "E177", {"center": v(244.6, 175.83) * mm, "radius": 2.24 * mm});
            skCircle(sketch, "E178", {"center": v(187.7, 129.86) * mm, "radius": 2.24 * mm});
            skCircle(sketch, "E179", {"center": v(141.72, 175.83) * mm, "radius": 2.24 * mm});
            skLineSegment(sketch, "E180.bottom", {"start": v(258.94, 204.15) * mm, "end": v(304.92, 204.15) * mm, "construction": true});
            skLineSegment(sketch, "E180.top", {"start": v(258.94, 250.13) * mm, "end": v(304.92, 250.13) * mm, "construction": true});
            skLineSegment(sketch, "E180.left", {"start": v(258.94, 204.15) * mm, "end": v(258.94, 250.13) * mm, "construction": true});
            skLineSegment(sketch, "E180.right", {"start": v(304.92, 204.15) * mm, "end": v(304.92, 250.13) * mm, "construction": true});
            skLineSegment(sketch, "E181.bottom", {"start": v(198.62, 204.15) * mm, "end": v(244.6, 204.15) * mm, "construction": true});
            skLineSegment(sketch, "E181.top", {"start": v(198.62, 250.13) * mm, "end": v(244.6, 250.13) * mm, "construction": true});
            skLineSegment(sketch, "E181.left", {"start": v(198.62, 204.15) * mm, "end": v(198.62, 250.13) * mm, "construction": true});
            skLineSegment(sketch, "E181.right", {"start": v(244.6, 204.15) * mm, "end": v(244.6, 250.13) * mm, "construction": true});
            skLineSegment(sketch, "E182.bottom", {"start": v(141.72, 204.15) * mm, "end": v(187.7, 204.15) * mm, "construction": true});
            skLineSegment(sketch, "E182.top", {"start": v(141.72, 250.13) * mm, "end": v(187.7, 250.13) * mm, "construction": true});
            skLineSegment(sketch, "E182.left", {"start": v(141.72, 204.15) * mm, "end": v(141.72, 250.13) * mm, "construction": true});
            skLineSegment(sketch, "E182.right", {"start": v(187.7, 204.15) * mm, "end": v(187.7, 250.13) * mm, "construction": true});
            skLineSegment(sketch, "E183.bottom", {"start": v(141.72, 275.4) * mm, "end": v(187.7, 275.4) * mm, "construction": true});
            skLineSegment(sketch, "E183.top", {"start": v(141.72, 321.37) * mm, "end": v(187.7, 321.37) * mm, "construction": true});
            skLineSegment(sketch, "E183.left", {"start": v(141.72, 275.4) * mm, "end": v(141.72, 321.37) * mm, "construction": true});
            skLineSegment(sketch, "E183.right", {"start": v(187.7, 275.4) * mm, "end": v(187.7, 321.37) * mm, "construction": true});
            skLineSegment(sketch, "E184.bottom", {"start": v(198.62, 275.4) * mm, "end": v(244.6, 275.4) * mm, "construction": true});
            skLineSegment(sketch, "E184.top", {"start": v(198.62, 321.37) * mm, "end": v(244.6, 321.37) * mm, "construction": true});
            skLineSegment(sketch, "E184.left", {"start": v(198.62, 275.4) * mm, "end": v(198.62, 321.37) * mm, "construction": true});
            skLineSegment(sketch, "E184.right", {"start": v(244.6, 275.4) * mm, "end": v(244.6, 321.37) * mm, "construction": true});
            skCircle(sketch, "E185", {"center": v(141.72, 321.37) * mm, "radius": 2.24 * mm});
            skCircle(sketch, "E186", {"center": v(187.7, 321.37) * mm, "radius": 2.24 * mm});
            skCircle(sketch, "E187", {"center": v(198.62, 321.37) * mm, "radius": 2.24 * mm});
            skCircle(sketch, "E188", {"center": v(141.72, 275.4) * mm, "radius": 2.24 * mm});
            skCircle(sketch, "E189", {"center": v(187.7, 275.4) * mm, "radius": 2.24 * mm});
            skCircle(sketch, "E190", {"center": v(244.6, 275.4) * mm, "radius": 2.24 * mm});
            skCircle(sketch, "E191", {"center": v(141.72, 204.15) * mm, "radius": 2.24 * mm});
            skCircle(sketch, "E192", {"center": v(187.7, 250.13) * mm, "radius": 2.24 * mm});
            skCircle(sketch, "E193", {"center": v(198.62, 250.13) * mm, "radius": 2.24 * mm});
            skCircle(sketch, "E194", {"center": v(244.6, 204.15) * mm, "radius": 2.24 * mm});
            skCircle(sketch, "E195", {"center": v(258.94, 250.13) * mm, "radius": 2.24 * mm});
            skCircle(sketch, "E196", {"center": v(304.92, 204.15) * mm, "radius": 2.24 * mm});
            skLineSegment(sketch, "E197.bottom", {"start": v(-229.12, 275.4) * mm, "end": v(-183.15, 275.4) * mm, "construction": true});
            skLineSegment(sketch, "E197.top", {"start": v(-229.12, 321.37) * mm, "end": v(-183.15, 321.37) * mm, "construction": true});
            skLineSegment(sketch, "E197.left", {"start": v(-229.12, 275.4) * mm, "end": v(-229.12, 321.37) * mm, "construction": true});
            skLineSegment(sketch, "E197.right", {"start": v(-183.15, 275.4) * mm, "end": v(-183.15, 321.37) * mm, "construction": true});
            skLineSegment(sketch, "E198.bottom", {"start": v(-229.12, 226.5) * mm, "end": v(-183.15, 226.5) * mm, "construction": true});
            skLineSegment(sketch, "E198.top", {"start": v(-229.12, 180.53) * mm, "end": v(-183.15, 180.53) * mm, "construction": true});
            skLineSegment(sketch, "E198.left", {"start": v(-229.12, 226.5) * mm, "end": v(-229.12, 180.53) * mm, "construction": true});
            skLineSegment(sketch, "E198.right", {"start": v(-183.15, 226.5) * mm, "end": v(-183.15, 180.53) * mm, "construction": true});
            skLineSegment(sketch, "E199.bottom", {"start": v(-229.12, 156.65) * mm, "end": v(-183.15, 156.65) * mm, "construction": true});
            skLineSegment(sketch, "E199.top", {"start": v(-229.12, 110.68) * mm, "end": v(-183.15, 110.68) * mm, "construction": true});
            skLineSegment(sketch, "E199.left", {"start": v(-229.12, 156.65) * mm, "end": v(-229.12, 110.68) * mm, "construction": true});
            skLineSegment(sketch, "E199.right", {"start": v(-183.15, 156.65) * mm, "end": v(-183.15, 110.68) * mm, "construction": true});
            skLineSegment(sketch, "E200.bottom", {"start": v(-243.09, 12.38) * mm, "end": v(-169.18, 12.38) * mm, "construction": true});
            skLineSegment(sketch, "E200.top", {"start": v(-243.09, 86.3) * mm, "end": v(-169.18, 86.3) * mm, "construction": true});
            skLineSegment(sketch, "E200.left", {"start": v(-243.09, 12.38) * mm, "end": v(-243.09, 86.3) * mm, "construction": true});
            skLineSegment(sketch, "E200.right", {"start": v(-169.18, 12.38) * mm, "end": v(-169.18, 86.3) * mm, "construction": true});
            skCircle(sketch, "E201", {"center": v(-243.09, 86.3) * mm, "radius": 2.24 * mm});
            skCircle(sketch, "E202", {"center": v(-169.18, 86.3) * mm, "radius": 2.24 * mm});
            skCircle(sketch, "E203", {"center": v(-243.09, 12.38) * mm, "radius": 2.24 * mm});
            skCircle(sketch, "E204", {"center": v(-169.18, 12.38) * mm, "radius": 2.24 * mm});
            skCircle(sketch, "E205", {"center": v(-183.15, 110.68) * mm, "radius": 2.24 * mm});
            skCircle(sketch, "E206", {"center": v(-183.15, 156.65) * mm, "radius": 2.24 * mm});
            skCircle(sketch, "E207", {"center": v(-229.12, 156.65) * mm, "radius": 2.24 * mm});
            skCircle(sketch, "E208", {"center": v(-229.12, 180.53) * mm, "radius": 2.24 * mm});
            skCircle(sketch, "E209", {"center": v(-183.15, 226.5) * mm, "radius": 2.24 * mm});
            skCircle(sketch, "E210", {"center": v(-229.12, 321.37) * mm, "radius": 2.24 * mm});
            skCircle(sketch, "E211", {"center": v(-183.15, 321.37) * mm, "radius": 2.24 * mm});
            skCircle(sketch, "E212", {"center": v(-183.15, 275.4) * mm, "radius": 2.24 * mm});
            skCircle(sketch, "E213", {"center": v(-229.12, 275.4) * mm, "radius": 2.24 * mm});
            skCircle(sketch, "E214", {"center": v(-134.89, 247.33) * mm, "radius": 2.24 * mm});
            skLineSegment(sketch, "E215", {"start": v(-134.89, 247.33) * mm, "end": v(113.27, 247.33) * mm, "construction": true});
            skLineSegment(sketch, "E216", {"start": v(-134.89, 247.33) * mm, "end": v(-134.89, 123.63) * mm, "construction": true});
            skLineSegment(sketch, "E217", {"start": v(-134.89, 126.94) * mm, "end": v(113.27, 126.94) * mm, "construction": true});
            skLineSegment(sketch, "E218", {"start": v(-23.38, 250.63) * mm, "end": v(-23.38, 126.94) * mm, "construction": true});
            skLineSegment(sketch, "E219", {"start": v(-1.54, 247.33) * mm, "end": v(-1.54, 126.94) * mm, "construction": true});
            skLineSegment(sketch, "E220", {"start": v(109.97, 247.33) * mm, "end": v(109.97, 126.94) * mm, "construction": true});
            skCircle(sketch, "E221", {"center": v(-134.89, 126.94) * mm, "radius": 2.24 * mm});
            skCircle(sketch, "E222", {"center": v(-23.38, 126.94) * mm, "radius": 2.24 * mm});
            skCircle(sketch, "E223", {"center": v(-23.38, 247.33) * mm, "radius": 2.24 * mm});
            skCircle(sketch, "E224", {"center": v(-1.54, 247.33) * mm, "radius": 2.24 * mm});
            skCircle(sketch, "E225", {"center": v(-1.54, 126.94) * mm, "radius": 2.24 * mm});
            skCircle(sketch, "E226", {"center": v(109.97, 247.33) * mm, "radius": 2.24 * mm});
            skCircle(sketch, "E227", {"center": v(109.97, 126.94) * mm, "radius": 2.24 * mm});
            skLineSegment(sketch, "E228", {"start": v(221.6, 190) * mm, "end": v(226.68, 190) * mm, "construction": true});
            skLineSegment(sketch, "E229", {"start": v(164.7, 190) * mm, "end": v(159.63, 190) * mm, "construction": true});
            skCircle(sketch, "E230", {"center": v(159.63, 190) * mm, "radius": 2.24 * mm});
            skCircle(sketch, "E231", {"center": v(226.68, 190) * mm, "radius": 2.24 * mm});
            skCircle(sketch, "E232", {"center": v(409.94, -119.7) * mm, "radius": 2.24 * mm});
            skCircle(sketch, "E233", {"center": v(435.34, -119.7) * mm, "radius": 2.24 * mm});
            skCircle(sketch, "E234", {"center": v(409.94, -53.66) * mm, "radius": 2.24 * mm});
            skCircle(sketch, "E235", {"center": v(435.34, -53.66) * mm, "radius": 2.24 * mm});
            skCircle(sketch, "E236.0.1.0", {"center": v(409.94, -43.5) * mm, "radius": 2.24 * mm});
            skCircle(sketch, "E236.0.1.1", {"center": v(435.34, -43.5) * mm, "radius": 2.24 * mm});
            skCircle(sketch, "E236.0.1.2", {"center": v(409.94, 22.54) * mm, "radius": 2.24 * mm});
            skCircle(sketch, "E236.0.1.3", {"center": v(435.34, 22.54) * mm, "radius": 2.24 * mm});
            skCircle(sketch, "E236.0.2.0", {"center": v(409.94, 32.7) * mm, "radius": 2.24 * mm});
            skCircle(sketch, "E236.0.2.1", {"center": v(435.34, 32.7) * mm, "radius": 2.24 * mm});
            skCircle(sketch, "E236.0.2.2", {"center": v(409.94, 98.74) * mm, "radius": 2.24 * mm});
            skCircle(sketch, "E236.0.2.3", {"center": v(435.34, 98.74) * mm, "radius": 2.24 * mm});
            skLineSegment(sketch, "E236.direction1", {"start": v(409.94, -119.7) * mm, "end": v(435.34, -119.7) * mm, "construction": true});
            skLineSegment(sketch, "E236.direction2", {"start": v(409.94, -119.7) * mm, "end": v(409.94, -43.5) * mm, "construction": true});
            skLineSegment(sketch, "E237", {"start": v(-104.2, 360.44) * mm, "end": v(74.83, 360.44) * mm, "construction": true});
            skPoint(sketch, "E238.endSnap0", {"position": v(-85.98, 277.2) * mm});
            skLineSegment(sketch, "E239", {"start": v(65.2, 369.89) * mm, "end": v(65.2, 261.85) * mm, "construction": true});
            skLineSegment(sketch, "E240", {"start": v(-102, 273.06) * mm, "end": v(74.83, 273.06) * mm, "construction": true});
            skLineSegment(sketch, "E241", {"start": v(-90.12, 360.44) * mm, "end": v(-90.12, 273.06) * mm, "construction": true});
            skCircle(sketch, "E242", {"center": v(-90.12, 360.44) * mm, "radius": 2.24 * mm});
            skCircle(sketch, "E243", {"center": v(65.2, 360.44) * mm, "radius": 2.24 * mm});
            skCircle(sketch, "E244", {"center": v(65.2, 273.06) * mm, "radius": 2.24 * mm});
            skCircle(sketch, "E245", {"center": v(-90.12, 273.06) * mm, "radius": 2.24 * mm});
            skCircle(sketch, "E246", {"center": v(-180.73, -13.53) * mm, "radius": 2.24 * mm});
            skCircle(sketch, "E247", {"center": v(-180.73, -85.92) * mm, "radius": 2.24 * mm});
            skLineSegment(sketch, "E248", {"start": v(-233.44, -13.85) * mm, "end": v(-233.44, -88.15) * mm, "construction": true});
            skCircle(sketch, "E249", {"center": v(-233.44, -13.53) * mm, "radius": 2.24 * mm});
            skCircle(sketch, "E250", {"center": v(-233.44, -85.92) * mm, "radius": 2.24 * mm});
            skLineSegment(sketch, "E251", {"start": v(-180.73, -85.92) * mm, "end": v(-180.73, -13.53) * mm, "construction": true});
            skLineSegment(sketch, "E252.bottom", {"start": v(169.9, -1.15) * mm, "end": v(171.7, -1.15) * mm, "construction": true});
            skLineSegment(sketch, "E252.top", {"start": v(169.9, -3.05) * mm, "end": v(171.7, -3.05) * mm, "construction": true});
            skLineSegment(sketch, "E252.left", {"start": v(169.9, -1.15) * mm, "end": v(169.9, -3.05) * mm, "construction": true});
            skLineSegment(sketch, "E252.right", {"start": v(171.7, -1.15) * mm, "end": v(171.7, -3.05) * mm, "construction": true});
            skPoint(sketch, "E252.middle", {"position": v(170.8, -2.1) * mm});
            skLineSegment(sketch, "E253", {"start": v(170.73, -1.15) * mm, "end": v(169.9, -1.15) * mm});
            skLineSegment(sketch, "E254", {"start": v(170.73, -3.05) * mm, "end": v(169.9, -3.05) * mm});
            skLineSegment(sketch, "E255", {"start": v(169.9, -3.05) * mm, "end": v(169.9, -1.15) * mm});
            skLineSegment(sketch, "E256.left", {"start": v(377.55, 3.93) * mm, "end": v(377.55, 2.03) * mm, "construction": true});
            skPoint(sketch, "E256.middle", {"position": v(378.45, 2.98) * mm});
            skLineSegment(sketch, "E257", {"start": v(378.38, 3.93) * mm, "end": v(377.55, 3.93) * mm});
            skLineSegment(sketch, "E258", {"start": v(378.38, 2.03) * mm, "end": v(377.55, 2.03) * mm});
            skLineSegment(sketch, "E259", {"start": v(377.55, 2.03) * mm, "end": v(377.55, 3.93) * mm});
            skLineSegment(sketch, "E260.bottom", {"start": v(-223.54, -115.45) * mm, "end": v(-221.74, -115.45) * mm, "construction": true});
            skLineSegment(sketch, "E260.top", {"start": v(-223.54, -117.35) * mm, "end": v(-221.74, -117.35) * mm, "construction": true});
            skLineSegment(sketch, "E260.left", {"start": v(-223.54, -115.45) * mm, "end": v(-223.54, -117.35) * mm, "construction": true});
            skLineSegment(sketch, "E260.right", {"start": v(-221.74, -115.45) * mm, "end": v(-221.74, -117.35) * mm, "construction": true});
            skPoint(sketch, "E260.middle", {"position": v(-222.64, -116.4) * mm});
            skLineSegment(sketch, "E261.bottom", {"start": v(-184.17, -115.45) * mm, "end": v(-182.37, -115.45) * mm, "construction": true});
            skLineSegment(sketch, "E261.top", {"start": v(-184.17, -117.35) * mm, "end": v(-182.37, -117.35) * mm, "construction": true});
            skLineSegment(sketch, "E261.left", {"start": v(-184.17, -115.45) * mm, "end": v(-184.17, -117.35) * mm, "construction": true});
            skLineSegment(sketch, "E261.right", {"start": v(-182.37, -115.45) * mm, "end": v(-182.37, -117.35) * mm, "construction": true});
            skPoint(sketch, "E261.middle", {"position": v(-183.27, -116.4) * mm});
            skLineSegment(sketch, "E262", {"start": v(-222.71, -115.45) * mm, "end": v(-223.54, -115.45) * mm});
            skLineSegment(sketch, "E263", {"start": v(-222.71, -117.35) * mm, "end": v(-223.54, -117.35) * mm});
            skLineSegment(sketch, "E264", {"start": v(-223.54, -115.45) * mm, "end": v(-223.54, -117.35) * mm});
            skLineSegment(sketch, "E265", {"start": v(-183.34, -115.45) * mm, "end": v(-184.17, -115.45) * mm});
            skLineSegment(sketch, "E266", {"start": v(-183.34, -117.35) * mm, "end": v(-184.17, -117.35) * mm});
            skLineSegment(sketch, "E267", {"start": v(-184.17, -115.45) * mm, "end": v(-184.17, -117.35) * mm});
            skLineSegment(sketch, "E268", {"start": v(332.98, 208.72) * mm, "end": v(339.08, 208.72) * mm, "construction": true});
            skLineSegment(sketch, "E269.bottom", {"start": v(338.18, 209.67) * mm, "end": v(339.98, 209.67) * mm, "construction": true});
            skLineSegment(sketch, "E269.top", {"start": v(338.18, 207.77) * mm, "end": v(339.98, 207.77) * mm, "construction": true});
            skLineSegment(sketch, "E269.left", {"start": v(338.18, 209.67) * mm, "end": v(338.18, 207.77) * mm, "construction": true});
            skLineSegment(sketch, "E269.right", {"start": v(339.98, 209.67) * mm, "end": v(339.98, 207.77) * mm, "construction": true});
            skPoint(sketch, "E269.middle", {"position": v(339.08, 208.72) * mm});
            skLineSegment(sketch, "E270", {"start": v(339, 209.67) * mm, "end": v(338.18, 209.67) * mm});
            skLineSegment(sketch, "E271", {"start": v(339, 207.77) * mm, "end": v(338.18, 207.77) * mm});
            skLineSegment(sketch, "E272", {"start": v(338.18, 207.77) * mm, "end": v(338.18, 209.67) * mm});
            skLineSegment(sketch, "E273.bottom", {"start": v(377.55, 181.73) * mm, "end": v(379.35, 181.73) * mm, "construction": true});
            skLineSegment(sketch, "E273.top", {"start": v(377.55, 179.83) * mm, "end": v(379.35, 179.83) * mm, "construction": true});
            skLineSegment(sketch, "E273.left", {"start": v(377.55, 181.73) * mm, "end": v(377.55, 179.83) * mm, "construction": true});
            skLineSegment(sketch, "E273.right", {"start": v(379.35, 181.73) * mm, "end": v(379.35, 179.83) * mm, "construction": true});
            skPoint(sketch, "E273.middle", {"position": v(378.45, 180.78) * mm});
            skLineSegment(sketch, "E274", {"start": v(378.38, 181.73) * mm, "end": v(377.55, 181.73) * mm});
            skLineSegment(sketch, "E275", {"start": v(378.38, 179.83) * mm, "end": v(377.55, 179.83) * mm});
            skLineSegment(sketch, "E276", {"start": v(377.55, 179.83) * mm, "end": v(377.55, 181.73) * mm});
            skLineSegment(sketch, "E277.bottom", {"start": v(377.55, 154.43) * mm, "end": v(379.35, 154.43) * mm, "construction": true});
            skLineSegment(sketch, "E277.top", {"start": v(377.55, 156.33) * mm, "end": v(379.35, 156.33) * mm, "construction": true});
            skLineSegment(sketch, "E277.left", {"start": v(377.55, 154.43) * mm, "end": v(377.55, 156.33) * mm, "construction": true});
            skLineSegment(sketch, "E277.right", {"start": v(379.35, 154.43) * mm, "end": v(379.35, 156.33) * mm, "construction": true});
            skPoint(sketch, "E277.middle", {"position": v(378.45, 155.38) * mm});
            skLineSegment(sketch, "E278.bottom", {"start": v(377.5, 129.03) * mm, "end": v(379.4, 129.03) * mm, "construction": true});
            skLineSegment(sketch, "E278.top", {"start": v(377.5, 130.93) * mm, "end": v(379.4, 130.93) * mm, "construction": true});
            skLineSegment(sketch, "E278.left", {"start": v(377.5, 129.03) * mm, "end": v(377.5, 130.93) * mm, "construction": true});
            skLineSegment(sketch, "E278.right", {"start": v(379.4, 129.03) * mm, "end": v(379.4, 130.93) * mm, "construction": true});
            skPoint(sketch, "E278.middle", {"position": v(378.45, 129.98) * mm});
            skLineSegment(sketch, "E279.bottom", {"start": v(377.55, 103.63) * mm, "end": v(379.35, 103.63) * mm, "construction": true});
            skLineSegment(sketch, "E279.top", {"start": v(377.55, 105.53) * mm, "end": v(379.35, 105.53) * mm, "construction": true});
            skLineSegment(sketch, "E279.left", {"start": v(377.55, 103.63) * mm, "end": v(377.55, 105.53) * mm, "construction": true});
            skLineSegment(sketch, "E279.right", {"start": v(379.35, 103.63) * mm, "end": v(379.35, 105.53) * mm, "construction": true});
            skPoint(sketch, "E279.middle", {"position": v(378.45, 104.58) * mm});
            skLineSegment(sketch, "E280", {"start": v(378.38, 156.33) * mm, "end": v(377.55, 156.33) * mm});
            skLineSegment(sketch, "E281", {"start": v(378.38, 154.43) * mm, "end": v(377.55, 154.43) * mm});
            skLineSegment(sketch, "E282", {"start": v(377.55, 154.43) * mm, "end": v(377.55, 156.33) * mm});
            skLineSegment(sketch, "E283", {"start": v(378.38, 130.93) * mm, "end": v(377.5, 130.93) * mm});
            skLineSegment(sketch, "E284", {"start": v(378.38, 129.03) * mm, "end": v(377.5, 129.03) * mm});
            skLineSegment(sketch, "E285", {"start": v(377.5, 129.03) * mm, "end": v(377.5, 130.93) * mm});
            skLineSegment(sketch, "E286", {"start": v(378.38, 105.53) * mm, "end": v(377.55, 105.53) * mm});
            skLineSegment(sketch, "E287", {"start": v(378.38, 103.63) * mm, "end": v(377.55, 103.63) * mm});
            skLineSegment(sketch, "E288", {"start": v(377.55, 103.63) * mm, "end": v(377.55, 105.53) * mm});
            skLineSegment(sketch, "E289.bottom", {"start": v(377.55, 80.13) * mm, "end": v(379.35, 80.13) * mm, "construction": true});
            skLineSegment(sketch, "E289.top", {"start": v(377.55, 78.23) * mm, "end": v(379.35, 78.23) * mm, "construction": true});
            skLineSegment(sketch, "E289.left", {"start": v(377.55, 80.13) * mm, "end": v(377.55, 78.23) * mm, "construction": true});
            skLineSegment(sketch, "E289.right", {"start": v(379.35, 80.13) * mm, "end": v(379.35, 78.23) * mm, "construction": true});
            skPoint(sketch, "E289.middle", {"position": v(378.45, 79.18) * mm});
            skLineSegment(sketch, "E290", {"start": v(378.38, 80.13) * mm, "end": v(377.55, 80.13) * mm});
            skLineSegment(sketch, "E291", {"start": v(378.38, 78.23) * mm, "end": v(377.55, 78.23) * mm});
            skLineSegment(sketch, "E292", {"start": v(377.55, 78.23) * mm, "end": v(377.55, 80.13) * mm});
            skLineSegment(sketch, "E293.bottom", {"start": v(377.55, 52.83) * mm, "end": v(379.35, 52.83) * mm, "construction": true});
            skLineSegment(sketch, "E293.top", {"start": v(377.55, 54.73) * mm, "end": v(379.35, 54.73) * mm, "construction": true});
            skLineSegment(sketch, "E293.left", {"start": v(377.55, 52.83) * mm, "end": v(377.55, 54.73) * mm, "construction": true});
            skLineSegment(sketch, "E293.right", {"start": v(379.35, 52.83) * mm, "end": v(379.35, 54.73) * mm, "construction": true});
            skPoint(sketch, "E293.middle", {"position": v(378.45, 53.78) * mm});
            skLineSegment(sketch, "E294", {"start": v(378.38, 54.73) * mm, "end": v(377.55, 54.73) * mm});
            skLineSegment(sketch, "E295", {"start": v(378.38, 52.83) * mm, "end": v(377.55, 52.83) * mm});
            skLineSegment(sketch, "E296", {"start": v(377.55, 54.73) * mm, "end": v(377.55, 52.83) * mm});
            skLineSegment(sketch, "E297.bottom", {"start": v(377.55, 27.43) * mm, "end": v(379.35, 27.43) * mm, "construction": true});
            skLineSegment(sketch, "E297.top", {"start": v(377.55, 29.33) * mm, "end": v(379.35, 29.33) * mm, "construction": true});
            skLineSegment(sketch, "E297.left", {"start": v(377.55, 27.43) * mm, "end": v(377.55, 29.33) * mm, "construction": true});
            skLineSegment(sketch, "E297.right", {"start": v(379.35, 27.43) * mm, "end": v(379.35, 29.33) * mm, "construction": true});
            skPoint(sketch, "E297.middle", {"position": v(378.45, 28.38) * mm});
            skLineSegment(sketch, "E298", {"start": v(378.38, 29.33) * mm, "end": v(377.55, 29.33) * mm});
            skLineSegment(sketch, "E299", {"start": v(378.38, 27.43) * mm, "end": v(377.55, 27.43) * mm});
            skLineSegment(sketch, "E300", {"start": v(377.55, 29.33) * mm, "end": v(377.55, 27.43) * mm});
            skLineSegment(sketch, "E301.bottom", {"start": v(287.13, -102.87) * mm, "end": v(288.93, -102.87) * mm, "construction": true});
            skLineSegment(sketch, "E301.top", {"start": v(287.13, -100.97) * mm, "end": v(288.93, -100.97) * mm, "construction": true});
            skLineSegment(sketch, "E301.left", {"start": v(287.13, -102.87) * mm, "end": v(287.13, -100.97) * mm, "construction": true});
            skLineSegment(sketch, "E301.right", {"start": v(288.93, -102.87) * mm, "end": v(288.93, -100.97) * mm, "construction": true});
            skPoint(sketch, "E301.middle", {"position": v(288.03, -101.92) * mm});
            skLineSegment(sketch, "E302.bottom", {"start": v(338.18, -102.87) * mm, "end": v(339.98, -102.87) * mm, "construction": true});
            skLineSegment(sketch, "E302.top", {"start": v(338.18, -100.97) * mm, "end": v(339.98, -100.97) * mm, "construction": true});
            skLineSegment(sketch, "E302.left", {"start": v(338.18, -102.87) * mm, "end": v(338.18, -100.97) * mm, "construction": true});
            skLineSegment(sketch, "E302.right", {"start": v(339.98, -102.87) * mm, "end": v(339.98, -100.97) * mm, "construction": true});
            skPoint(sketch, "E302.middle", {"position": v(339.08, -101.92) * mm});
            skLineSegment(sketch, "E303.bottom", {"start": v(377.55, -102.87) * mm, "end": v(379.35, -102.87) * mm, "construction": true});
            skLineSegment(sketch, "E303.top", {"start": v(377.55, -100.97) * mm, "end": v(379.35, -100.97) * mm, "construction": true});
            skLineSegment(sketch, "E303.left", {"start": v(377.55, -102.87) * mm, "end": v(377.55, -100.97) * mm, "construction": true});
            skLineSegment(sketch, "E303.right", {"start": v(379.35, -102.87) * mm, "end": v(379.35, -100.97) * mm, "construction": true});
            skPoint(sketch, "E303.middle", {"position": v(378.45, -101.92) * mm});
            skLineSegment(sketch, "E304", {"start": v(287.95, -100.97) * mm, "end": v(287.13, -100.97) * mm});
            skLineSegment(sketch, "E305", {"start": v(287.95, -102.87) * mm, "end": v(287.13, -102.87) * mm});
            skLineSegment(sketch, "E306", {"start": v(287.13, -100.97) * mm, "end": v(287.13, -102.87) * mm});
            skLineSegment(sketch, "E307", {"start": v(339, -100.97) * mm, "end": v(338.18, -100.97) * mm});
            skLineSegment(sketch, "E308", {"start": v(339, -102.87) * mm, "end": v(338.18, -102.87) * mm});
            skLineSegment(sketch, "E309", {"start": v(338.18, -100.97) * mm, "end": v(338.18, -102.87) * mm});
            skLineSegment(sketch, "E310", {"start": v(378.38, -100.97) * mm, "end": v(377.55, -100.97) * mm});
            skLineSegment(sketch, "E311", {"start": v(378.38, -102.87) * mm, "end": v(377.55, -102.87) * mm});
            skLineSegment(sketch, "E312", {"start": v(377.55, -100.97) * mm, "end": v(377.55, -102.87) * mm});
            skLineSegment(sketch, "E313.bottom", {"start": v(349.1, -69.6) * mm, "end": v(350.9, -69.6) * mm, "construction": true});
            skLineSegment(sketch, "E313.top", {"start": v(349.1, -67.7) * mm, "end": v(350.9, -67.7) * mm, "construction": true});
            skLineSegment(sketch, "E313.left", {"start": v(349.1, -69.6) * mm, "end": v(349.1, -67.7) * mm, "construction": true});
            skLineSegment(sketch, "E313.right", {"start": v(350.9, -69.6) * mm, "end": v(350.9, -67.7) * mm, "construction": true});
            skPoint(sketch, "E313.middle", {"position": v(350, -68.64) * mm});
            skLineSegment(sketch, "E314", {"start": v(349.93, -67.7) * mm, "end": v(349.1, -67.7) * mm});
            skLineSegment(sketch, "E315", {"start": v(349.93, -69.6) * mm, "end": v(349.1, -69.6) * mm});
            skLineSegment(sketch, "E316", {"start": v(349.1, -67.7) * mm, "end": v(349.1, -69.6) * mm});
            skLineSegment(sketch, "E317.bottom", {"start": v(287.13, -50.54) * mm, "end": v(288.93, -50.54) * mm, "construction": true});
            skLineSegment(sketch, "E317.top", {"start": v(287.13, -48.64) * mm, "end": v(288.93, -48.64) * mm, "construction": true});
            skLineSegment(sketch, "E317.left", {"start": v(287.13, -50.54) * mm, "end": v(287.13, -48.64) * mm, "construction": true});
            skLineSegment(sketch, "E317.right", {"start": v(288.93, -50.54) * mm, "end": v(288.93, -48.64) * mm, "construction": true});
            skPoint(sketch, "E317.middle", {"position": v(288.03, -49.6) * mm});
            skLineSegment(sketch, "E318", {"start": v(287.95, -48.64) * mm, "end": v(287.13, -48.64) * mm});
            skLineSegment(sketch, "E319", {"start": v(287.95, -50.54) * mm, "end": v(287.13, -50.54) * mm});
            skLineSegment(sketch, "E320", {"start": v(287.13, -48.64) * mm, "end": v(287.13, -50.54) * mm});
            skLineSegment(sketch, "E321.bottom", {"start": v(287.13, 16.77) * mm, "end": v(288.93, 16.77) * mm, "construction": true});
            skLineSegment(sketch, "E321.top", {"start": v(287.13, 18.67) * mm, "end": v(288.93, 18.67) * mm, "construction": true});
            skLineSegment(sketch, "E321.left", {"start": v(287.13, 16.77) * mm, "end": v(287.13, 18.67) * mm, "construction": true});
            skLineSegment(sketch, "E321.right", {"start": v(288.93, 16.77) * mm, "end": v(288.93, 18.67) * mm, "construction": true});
            skPoint(sketch, "E321.middle", {"position": v(288.03, 17.72) * mm});
            skLineSegment(sketch, "E322", {"start": v(287.95, 18.67) * mm, "end": v(287.13, 18.67) * mm});
            skLineSegment(sketch, "E323", {"start": v(287.95, 16.77) * mm, "end": v(287.13, 16.77) * mm});
            skLineSegment(sketch, "E324", {"start": v(287.13, 18.67) * mm, "end": v(287.13, 16.77) * mm});
            skLineSegment(sketch, "E325.bottom", {"start": v(287.13, 70.1) * mm, "end": v(288.93, 70.1) * mm, "construction": true});
            skLineSegment(sketch, "E325.top", {"start": v(287.13, 72) * mm, "end": v(288.93, 72) * mm, "construction": true});
            skLineSegment(sketch, "E325.left", {"start": v(287.13, 70.1) * mm, "end": v(287.13, 72) * mm, "construction": true});
            skLineSegment(sketch, "E325.right", {"start": v(288.93, 70.1) * mm, "end": v(288.93, 72) * mm, "construction": true});
            skPoint(sketch, "E325.middle", {"position": v(288.03, 71.06) * mm});
            skLineSegment(sketch, "E326", {"start": v(287.95, 72) * mm, "end": v(287.13, 72) * mm});
            skLineSegment(sketch, "E327", {"start": v(287.95, 70.1) * mm, "end": v(287.13, 70.1) * mm});
            skLineSegment(sketch, "E328", {"start": v(287.13, 72) * mm, "end": v(287.13, 70.1) * mm});
            skLineSegment(sketch, "E329.bottom", {"start": v(287.13, 132.34) * mm, "end": v(287.95, 132.34) * mm});
            skLineSegment(sketch, "E329.top", {"start": v(287.13, 134.24) * mm, "end": v(287.95, 134.24) * mm});
            skLineSegment(sketch, "E329.left", {"start": v(287.13, 132.34) * mm, "end": v(287.13, 134.24) * mm});
            skPoint(sketch, "E329.middle", {"position": v(288.03, 133.29) * mm});
            skPoint(sketch, "E329.right.end.orphan", {"position": v(288.93, 134.24) * mm});
            skPoint(sketch, "E330.orphan", {"position": v(288.93, 132.34) * mm});
            skLineSegment(sketch, "E331.bottom", {"start": v(287.13, 168.66) * mm, "end": v(287.95, 168.66) * mm});
            skLineSegment(sketch, "E331.top", {"start": v(287.13, 170.56) * mm, "end": v(287.95, 170.56) * mm});
            skLineSegment(sketch, "E331.left", {"start": v(287.13, 168.66) * mm, "end": v(287.13, 170.56) * mm});
            skPoint(sketch, "E331.middle", {"position": v(288.03, 169.6) * mm});
            skPoint(sketch, "E331.right.end.orphan", {"position": v(288.93, 170.56) * mm});
            skPoint(sketch, "E332.orphan", {"position": v(288.93, 168.66) * mm});
            skLineSegment(sketch, "E333.bottom", {"start": v(198.36, 189.04) * mm, "end": v(199.18, 189.04) * mm});
            skLineSegment(sketch, "E333.top", {"start": v(198.36, 190.94) * mm, "end": v(199.18, 190.94) * mm});
            skLineSegment(sketch, "E333.left", {"start": v(198.36, 189.04) * mm, "end": v(198.36, 190.94) * mm});
            skPoint(sketch, "E333.middle", {"position": v(199.26, 190) * mm});
            skPoint(sketch, "E334.orphan", {"position": v(200.16, 190.94) * mm});
            skPoint(sketch, "E333.right.start.orphan", {"position": v(200.16, 189.04) * mm});
            skLineSegment(sketch, "E335.bottom", {"start": v(226.8, 40.13) * mm, "end": v(227.63, 40.13) * mm});
            skLineSegment(sketch, "E335.top", {"start": v(226.8, 42.03) * mm, "end": v(227.63, 42.03) * mm});
            skLineSegment(sketch, "E335.left", {"start": v(226.8, 40.13) * mm, "end": v(226.8, 42.03) * mm});
            skPoint(sketch, "E335.middle", {"position": v(227.7, 41.08) * mm});
            skPoint(sketch, "E336.orphan", {"position": v(228.6, 42.03) * mm});
            skPoint(sketch, "E337.orphan", {"position": v(228.6, 40.13) * mm});
            skLineSegment(sketch, "E338.bottom", {"start": v(169.9, -50.54) * mm, "end": v(171.7, -50.54) * mm, "construction": true});
            skLineSegment(sketch, "E338.top", {"start": v(169.9, -48.64) * mm, "end": v(171.7, -48.64) * mm, "construction": true});
            skLineSegment(sketch, "E338.left", {"start": v(169.9, -50.54) * mm, "end": v(169.9, -48.64) * mm, "construction": true});
            skLineSegment(sketch, "E338.right", {"start": v(171.7, -50.54) * mm, "end": v(171.7, -48.64) * mm, "construction": true});
            skPoint(sketch, "E338.middle", {"position": v(170.8, -49.6) * mm});
            skLineSegment(sketch, "E339", {"start": v(170.73, -48.64) * mm, "end": v(169.9, -48.64) * mm});
            skLineSegment(sketch, "E340", {"start": v(170.73, -50.54) * mm, "end": v(169.9, -50.54) * mm});
            skLineSegment(sketch, "E341", {"start": v(169.9, -48.64) * mm, "end": v(169.9, -50.54) * mm});
            skLineSegment(sketch, "E342.bottom", {"start": v(226.8, -50.54) * mm, "end": v(228.6, -50.54) * mm, "construction": true});
            skLineSegment(sketch, "E342.top", {"start": v(226.8, -48.64) * mm, "end": v(228.6, -48.64) * mm, "construction": true});
            skLineSegment(sketch, "E342.left", {"start": v(226.8, -50.54) * mm, "end": v(226.8, -48.64) * mm, "construction": true});
            skLineSegment(sketch, "E342.right", {"start": v(228.6, -50.54) * mm, "end": v(228.6, -48.64) * mm, "construction": true});
            skPoint(sketch, "E342.middle", {"position": v(227.7, -49.6) * mm});
            skLineSegment(sketch, "E343", {"start": v(227.63, -48.64) * mm, "end": v(226.8, -48.64) * mm});
            skLineSegment(sketch, "E344", {"start": v(227.63, -50.54) * mm, "end": v(226.8, -50.54) * mm});
            skLineSegment(sketch, "E345", {"start": v(226.8, -48.64) * mm, "end": v(226.8, -50.54) * mm});
            skLineSegment(sketch, "E346.bottom", {"start": v(244.08, -94.49) * mm, "end": v(245.88, -94.49) * mm, "construction": true});
            skLineSegment(sketch, "E346.top", {"start": v(244.08, -92.59) * mm, "end": v(245.88, -92.59) * mm, "construction": true});
            skLineSegment(sketch, "E346.left", {"start": v(244.08, -94.49) * mm, "end": v(244.08, -92.59) * mm, "construction": true});
            skLineSegment(sketch, "E346.right", {"start": v(245.88, -94.49) * mm, "end": v(245.88, -92.59) * mm, "construction": true});
            skPoint(sketch, "E346.middle", {"position": v(244.98, -93.54) * mm});
            skLineSegment(sketch, "E347", {"start": v(244.9, -92.59) * mm, "end": v(244.08, -92.59) * mm});
            skLineSegment(sketch, "E348", {"start": v(244.9, -94.49) * mm, "end": v(244.08, -94.49) * mm});
            skLineSegment(sketch, "E349", {"start": v(244.08, -92.59) * mm, "end": v(244.08, -94.49) * mm});
            skLineSegment(sketch, "E350", {"start": v(-240.3, 370.86) * mm, "end": v(-182.1, 390.14) * mm, "construction": true});
            skCircle(sketch, "E351", {"center": v(-211.2, 380.5) * mm, "radius": 2.24 * mm});
            skCircle(sketch, "E352", {"center": v(-238.47, 371.47) * mm, "radius": 2.24 * mm});
            skCircle(sketch, "E353", {"center": v(-184.03, 389.5) * mm, "radius": 2.24 * mm});
            skLineSegment(sketch, "E354", {"start": v(-134.89, 267.79) * mm, "end": v(-134.89, 367.74) * mm, "construction": true});
            skCircle(sketch, "E355", {"center": v(-134.89, 360.44) * mm, "radius": 2.24 * mm});
            skCircle(sketch, "E356", {"center": v(-134.89, 273.06) * mm, "radius": 2.24 * mm});
            skCircle(sketch, "E357", {"center": v(-124.4, 282.55) * mm, "radius": 2.24 * mm});
            skCircle(sketch, "E358", {"center": v(-124.4, 296.52) * mm, "radius": 2.24 * mm});
            skCircle(sketch, "E359", {"center": v(98.67, 321.37) * mm, "radius": 2.24 * mm});
            skCircle(sketch, "E360", {"center": v(98.67, 335.34) * mm, "radius": 2.24 * mm});
            skCircle(sketch, "E361", {"center": v(91.34, 347.03) * mm, "radius": 2.24 * mm});
            skCircle(sketch, "E362", {"center": v(104.18, 357.97) * mm, "radius": 2.24 * mm});
            skLineSegment(sketch, "E363", {"start": v(409.94, 98.74) * mm, "end": v(435.34, 98.74) * mm, "construction": true});
            skLineSegment(sketch, "E364", {"start": v(422.64, 98.74) * mm, "end": v(422.64, 112.88) * mm, "construction": true});
            skLineSegment(sketch, "E365", {"start": v(398.77, 91.12) * mm, "end": v(446.52, 91.12) * mm});
            skLineSegment(sketch, "E366", {"start": v(398.77, 40.32) * mm, "end": v(446.52, 40.32) * mm});
            skCircle(sketch, "E367", {"center": v(422.64, 103.82) * mm, "radius": 2.24 * mm});
            skLineSegment(sketch, "E368", {"start": v(398.77, -35.88) * mm, "end": v(446.52, -35.88) * mm});
            skLineSegment(sketch, "E369", {"start": v(398.77, 14.92) * mm, "end": v(446.52, 14.92) * mm});
            skLineSegment(sketch, "E370", {"start": v(421.12, -61.28) * mm, "end": v(446.52, -61.28) * mm});
            skLineSegment(sketch, "E371", {"start": v(421.12, -112.08) * mm, "end": v(446.52, -112.08) * mm});
            skSolve(sketch);
        }
        {
            var Q0;
            Q0=qSketchRegion(id+"F0",true);
            extrude(context, id + "F1", {"entities" : qUnion([Q0]), "depth" : 6 * mm});
        }
    });
